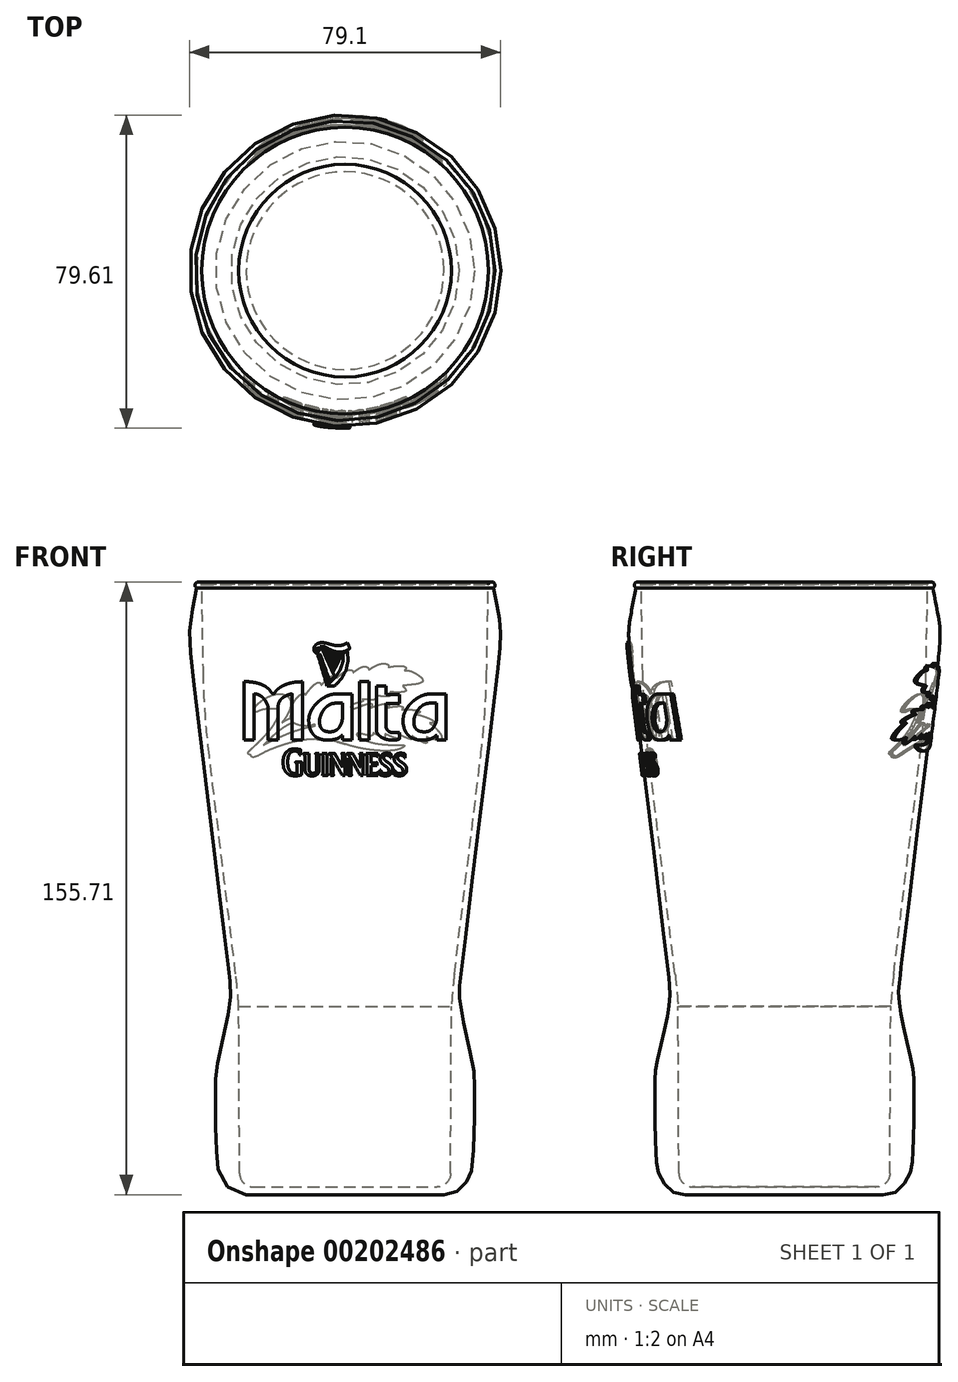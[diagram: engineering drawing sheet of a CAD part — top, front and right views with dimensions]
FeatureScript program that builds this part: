
annotation { "Feature Type Name" : "Feature", "Feature Type Description" : "" }
export const myFeature = defineFeature(function(context is Context, id is Id, definition is map)
    precondition{}
    {
        {
            var Q0;
            Q0=qCreatedBy(makeId("Front.planeOp"),FACE);
            var sketch = newSketch(context, id + "F0", { "sketchPlane" : qUnion([Q0])});
            skFitSpline(sketch, "E0", {"points": [v(-37.5, 79.86) * mm, v(-38.83, 73.29) * mm, v(-39.48, 68.91) * mm, v(-39.44, 64.6) * mm, v(-37.47, 47.15) * mm, v(-29.43, -19.33) * mm, v(-29.13, -22.16) * mm, v(-29.12, -25.92) * mm, v(-32.44, -42) * mm, v(-32.9, -47.3) * mm, v(-32.5, -66.8) * mm, v(-31.33, -71.06) * mm, v(-28.88, -74.03) * mm, v(-25.1, -75.12) * mm], "startDerivative": vector(-35.73, -160.8) * mm, "endDerivative": vector(111.11, -2.76) * mm});
            skLineSegment(sketch, "E1", {"start": v(-37.5, 79.86) * mm, "end": v(0, 79.86) * mm});
            skLineSegment(sketch, "E2", {"start": v(0, 79.86) * mm, "end": v(0, -75.12) * mm});
            skLineSegment(sketch, "E3", {"start": v(0, -75.12) * mm, "end": v(-25.1, -75.12) * mm});
            skSolve(sketch);
        }
        {
            var Q0;
            Q0=makeQuery(id+"F0.imprint","IMPRINT",FACE,{"disambiguationData":[TD([[makeQuery(id+"F0.imprint","IMPRINT",EDGE,{"derivedFrom":sQuery(id+"F0.wireOp",EDGE,"E0")}),1.0]])]});
            var Q1;
            Q1=sQuery(id+"F0.wireOp",EDGE,"E2");
            revolve(context, id + "F1", {"entities" : qUnion([Q0]), "axis" : qUnion([Q1]), "revolveType" : RevolveType.FULL});
        }
        {
            var Q0;
            Q0=qCreatedBy(makeId("Front.planeOp"),FACE);
            var sketch = newSketch(context, id + "F2", { "sketchPlane" : qUnion([Q0])});
            skLineSegment(sketch, "E4", {"start": v(0, 85.35) * mm, "end": v(-36.5, 85.35) * mm});
            skLineSegment(sketch, "E5", {"start": v(0, -73.16) * mm, "end": v(-23.31, -73.16) * mm});
            skLineSegment(sketch, "E6", {"start": v(0, 85.35) * mm, "end": v(0, -73.16) * mm});
            skLineSegment(sketch, "E7", {"start": v(-27.01, -27.28) * mm, "end": v(-26.8, -69.68) * mm});
            skLineSegment(sketch, "E8", {"start": v(-35.97, 56.7) * mm, "end": v(-36.5, 85.35) * mm});
            skLineSegment(sketch, "E9", {"start": v(-27.77, -19.08) * mm, "end": v(-34.48, 36.36) * mm});
            skArc(sketch, "E10", {"start": v(-27.01, -27.28) * mm, "mid": v(-27.34, -23.18) * mm, "end": v(-27.77, -19.08) * mm});
            skArc(sketch, "E11", {"start": v(-35.97, 56.7) * mm, "mid": v(-35.46, 46.51) * mm, "end": v(-34.48, 36.36) * mm});
            skPoint(sketch, "E12.visualSharp", {"position": v(-26.8, -73.16) * mm});
            skArc(sketch, "E12.filletArc", {"start": v(-26.8, -69.68) * mm, "mid": v(-25.78, -72.14) * mm, "end": v(-23.31, -73.16) * mm});
            skPoint(sketch, "E13.start.orphan", {"position": v(0, -75.16) * mm});
            skLineSegment(sketch, "E14", {"start": v(9.18, 85.35) * mm, "end": v(9.18, 79.96) * mm});
            skSolve(sketch);
        }
        {
            var Q0;
            Q0=qCreatedBy(makeId("Front.planeOp"),FACE);
            cPlane(context, id + "F3", {"entities" : qUnion([Q0]), "cplaneType" : CPlaneType.OFFSET, "offset" : 50 * mm, "width" : 150 * mm, "height" : 150 * mm});
        }
        {
            var Q0;
            Q0=makeQuery(id+"F2.imprint","IMPRINT",FACE,{"disambiguationData":[TD([[makeQuery(id+"F2.imprint","IMPRINT",EDGE,{"derivedFrom":sQuery(id+"F2.wireOp",EDGE,"E4")}),1.0]])]});
            var Q1;
            Q1=sQuery(id+"F2.wireOp",EDGE,"E6");
            revolve(context, id + "F4", {"operationType" : NewBodyOperationType.REMOVE, "entities" : qUnion([Q0]), "axis" : qUnion([Q1]), "revolveType" : RevolveType.FULL, "oppositeDirection" : true});
        }
        {
            var Q0;
            Q0=qCreatedBy(makeId("Front.planeOp"),FACE);
            var sketch = newSketch(context, id + "F5", { "sketchPlane" : qUnion([Q0])});
            skLineSegment(sketch, "E15", {"start": v(0, 79.96) * mm, "end": v(0, 86.28) * mm});
            skCircle(sketch, "E16", {"center": v(-37.25, 79.73) * mm, "radius": 0.85 * mm});
            skPoint(sketch, "E16.first.point", {"position": v(-36.4, 79.83) * mm});
            skPoint(sketch, "E16.second.point", {"position": v(-38.07, 79.5) * mm});
            skPoint(sketch, "E16.third.point", {"position": v(-38.1, 79.73) * mm});
            skSolve(sketch);
        }
        {
            var Q0;
            Q0=makeQuery(id+"F5.imprint","IMPRINT",FACE,{"disambiguationData":[TD([[makeQuery(id+"F5.imprint","IMPRINT",EDGE,{"derivedFrom":sQuery(id+"F5.wireOp",EDGE,"E16")}),1.0]])]});
            var Q1;
            Q1=sQuery(id+"F5.wireOp",EDGE,"E15");
            revolve(context, id + "F6", {"operationType" : NewBodyOperationType.ADD, "entities" : qUnion([Q0]), "axis" : qUnion([Q1]), "revolveType" : RevolveType.FULL});
        }
        {
            var Q0;
            Q0=qCreatedBy(makeId("Front.planeOp"),FACE);
            cPlane(context, id + "F7", {"entities" : qUnion([Q0]), "cplaneType" : CPlaneType.OFFSET, "offset" : 50 * mm, "oppositeDirection" : true, "width" : 150 * mm, "height" : 150 * mm});
        }
        {
            var Q0;
            Q0=qCreatedBy(id+"F3.planeOp",FACE);
            var sketch = newSketch(context, id + "F8", { "sketchPlane" : qUnion([Q0])});
            skLineSegment(sketch, "E17", {"start": v(-18.04, 52.15) * mm, "end": v(-18.51, 52.15) * mm});
            skLineSegment(sketch, "E18", {"start": v(-18.51, 52.15) * mm, "end": v(-19.27, 53.26) * mm});
            skLineSegment(sketch, "E19", {"start": v(-19.27, 53.26) * mm, "end": v(-20.3, 54.06) * mm});
            skLineSegment(sketch, "E20", {"start": v(-20.3, 54.06) * mm, "end": v(-21.46, 54.62) * mm});
            skLineSegment(sketch, "E21", {"start": v(-21.46, 54.62) * mm, "end": v(-22.68, 54.96) * mm});
            skLineSegment(sketch, "E22", {"start": v(-22.68, 54.96) * mm, "end": v(-23.82, 55.15) * mm});
            skLineSegment(sketch, "E23", {"start": v(-23.82, 55.15) * mm, "end": v(-24.77, 55.23) * mm});
            skLineSegment(sketch, "E24", {"start": v(-24.77, 55.23) * mm, "end": v(-25.42, 55.24) * mm});
            skLineSegment(sketch, "E25", {"start": v(-25.42, 55.24) * mm, "end": v(-25.66, 55.23) * mm});
            skLineSegment(sketch, "E26", {"start": v(-25.66, 55.23) * mm, "end": v(-25.66, 40.36) * mm});
            skLineSegment(sketch, "E27", {"start": v(-25.66, 40.36) * mm, "end": v(-23.13, 40.36) * mm});
            skLineSegment(sketch, "E28", {"start": v(-23.13, 40.36) * mm, "end": v(-23.13, 52.15) * mm});
            skLineSegment(sketch, "E29", {"start": v(-23.13, 52.15) * mm, "end": v(-22.2, 52) * mm});
            skLineSegment(sketch, "E30", {"start": v(-22.2, 52) * mm, "end": v(-21.43, 51.64) * mm});
            skLineSegment(sketch, "E31", {"start": v(-21.43, 51.64) * mm, "end": v(-20.8, 51.11) * mm});
            skLineSegment(sketch, "E32", {"start": v(-20.8, 51.11) * mm, "end": v(-20.33, 50.5) * mm});
            skLineSegment(sketch, "E33", {"start": v(-20.33, 50.5) * mm, "end": v(-19.97, 49.9) * mm});
            skLineSegment(sketch, "E34", {"start": v(-19.97, 49.9) * mm, "end": v(-19.74, 49.38) * mm});
            skLineSegment(sketch, "E35", {"start": v(-19.74, 49.38) * mm, "end": v(-19.6, 49) * mm});
            skLineSegment(sketch, "E36", {"start": v(-19.6, 49) * mm, "end": v(-19.56, 48.86) * mm});
            skLineSegment(sketch, "E37", {"start": v(-19.56, 48.86) * mm, "end": v(-19.56, 40.36) * mm});
            skLineSegment(sketch, "E38", {"start": v(-19.56, 40.36) * mm, "end": v(-17.05, 40.36) * mm});
            skLineSegment(sketch, "E39", {"start": v(-17.05, 40.36) * mm, "end": v(-17.05, 48.8) * mm});
            skLineSegment(sketch, "E40", {"start": v(-17.05, 48.8) * mm, "end": v(-16.9, 49.75) * mm});
            skLineSegment(sketch, "E41", {"start": v(-16.9, 49.75) * mm, "end": v(-16.5, 50.5) * mm});
            skLineSegment(sketch, "E42", {"start": v(-16.5, 50.5) * mm, "end": v(-15.91, 51.08) * mm});
            skLineSegment(sketch, "E43", {"start": v(-15.91, 51.08) * mm, "end": v(-15.25, 51.52) * mm});
            skLineSegment(sketch, "E44", {"start": v(-15.25, 51.52) * mm, "end": v(-14.6, 51.82) * mm});
            skLineSegment(sketch, "E45", {"start": v(-14.6, 51.82) * mm, "end": v(-14.01, 52.02) * mm});
            skLineSegment(sketch, "E46", {"start": v(-14.01, 52.02) * mm, "end": v(-13.6, 52.12) * mm});
            skLineSegment(sketch, "E47", {"start": v(-13.6, 52.12) * mm, "end": v(-13.45, 52.15) * mm});
            skLineSegment(sketch, "E48", {"start": v(-13.45, 52.15) * mm, "end": v(-13.45, 40.36) * mm});
            skLineSegment(sketch, "E49", {"start": v(-13.45, 40.36) * mm, "end": v(-10.79, 40.36) * mm});
            skLineSegment(sketch, "E50", {"start": v(-10.79, 40.36) * mm, "end": v(-10.79, 55.23) * mm});
            skLineSegment(sketch, "E51", {"start": v(-10.79, 55.23) * mm, "end": v(-12.8, 55.1) * mm});
            skLineSegment(sketch, "E52", {"start": v(-12.8, 55.1) * mm, "end": v(-14.41, 54.75) * mm});
            skLineSegment(sketch, "E53", {"start": v(-14.41, 54.75) * mm, "end": v(-15.68, 54.26) * mm});
            skLineSegment(sketch, "E54", {"start": v(-15.68, 54.26) * mm, "end": v(-16.63, 53.69) * mm});
            skLineSegment(sketch, "E55", {"start": v(-16.63, 53.69) * mm, "end": v(-17.3, 53.12) * mm});
            skLineSegment(sketch, "E56", {"start": v(-17.3, 53.12) * mm, "end": v(-17.74, 52.63) * mm});
            skLineSegment(sketch, "E57", {"start": v(-17.74, 52.63) * mm, "end": v(-17.97, 52.28) * mm});
            skLineSegment(sketch, "E58", {"start": v(-17.97, 52.28) * mm, "end": v(-18.04, 52.15) * mm});
            skLineSegment(sketch, "E59", {"start": v(-6.48, 45.4) * mm, "end": v(-6.43, 45.82) * mm});
            skLineSegment(sketch, "E60", {"start": v(-6.43, 45.82) * mm, "end": v(-6.26, 46.43) * mm});
            skLineSegment(sketch, "E61", {"start": v(-6.26, 46.43) * mm, "end": v(-5.97, 47.15) * mm});
            skLineSegment(sketch, "E62", {"start": v(-5.97, 47.15) * mm, "end": v(-5.54, 47.91) * mm});
            skLineSegment(sketch, "E63", {"start": v(-5.54, 47.91) * mm, "end": v(-4.96, 48.63) * mm});
            skLineSegment(sketch, "E64", {"start": v(-4.96, 48.63) * mm, "end": v(-4.23, 49.23) * mm});
            skLineSegment(sketch, "E65", {"start": v(-4.23, 49.23) * mm, "end": v(-3.33, 49.65) * mm});
            skLineSegment(sketch, "E66", {"start": v(-3.33, 49.65) * mm, "end": v(-2.26, 49.8) * mm});
            skLineSegment(sketch, "E67", {"start": v(-2.26, 49.8) * mm, "end": v(-0.67, 49.8) * mm});
            skLineSegment(sketch, "E68", {"start": v(-0.67, 49.8) * mm, "end": v(-0.67, 45.91) * mm});
            skLineSegment(sketch, "E69", {"start": v(-0.67, 45.91) * mm, "end": v(-0.68, 45.77) * mm});
            skLineSegment(sketch, "E70", {"start": v(-0.68, 45.77) * mm, "end": v(-0.75, 45.37) * mm});
            skLineSegment(sketch, "E71", {"start": v(-0.75, 45.37) * mm, "end": v(-0.9, 44.82) * mm});
            skLineSegment(sketch, "E72", {"start": v(-0.9, 44.82) * mm, "end": v(-1.14, 44.18) * mm});
            skLineSegment(sketch, "E73", {"start": v(-1.14, 44.18) * mm, "end": v(-1.53, 43.54) * mm});
            skLineSegment(sketch, "E74", {"start": v(-1.53, 43.54) * mm, "end": v(-2.07, 42.99) * mm});
            skLineSegment(sketch, "E75", {"start": v(-2.07, 42.99) * mm, "end": v(-2.81, 42.6) * mm});
            skLineSegment(sketch, "E76", {"start": v(-2.81, 42.6) * mm, "end": v(-3.77, 42.44) * mm});
            skLineSegment(sketch, "E77", {"start": v(-3.77, 42.44) * mm, "end": v(-4.71, 42.54) * mm});
            skLineSegment(sketch, "E78", {"start": v(-4.71, 42.54) * mm, "end": v(-5.4, 42.79) * mm});
            skLineSegment(sketch, "E79", {"start": v(-5.4, 42.79) * mm, "end": v(-5.9, 43.16) * mm});
            skLineSegment(sketch, "E80", {"start": v(-5.9, 43.16) * mm, "end": v(-6.2, 43.6) * mm});
            skLineSegment(sketch, "E81", {"start": v(-6.2, 43.6) * mm, "end": v(-6.38, 44.1) * mm});
            skLineSegment(sketch, "E82", {"start": v(-6.38, 44.1) * mm, "end": v(-6.46, 44.58) * mm});
            skLineSegment(sketch, "E83", {"start": v(-6.46, 44.58) * mm, "end": v(-6.49, 45.03) * mm});
            skLineSegment(sketch, "E84", {"start": v(-6.49, 45.03) * mm, "end": v(-6.48, 45.4) * mm});
            skLineSegment(sketch, "E85", {"start": v(-4.48, 40.35) * mm, "end": v(-3.5, 40.4) * mm});
            skLineSegment(sketch, "E86", {"start": v(-3.5, 40.4) * mm, "end": v(-2.73, 40.53) * mm});
            skLineSegment(sketch, "E87", {"start": v(-2.73, 40.53) * mm, "end": v(-2.11, 40.72) * mm});
            skLineSegment(sketch, "E88", {"start": v(-2.11, 40.72) * mm, "end": v(-1.65, 40.93) * mm});
            skLineSegment(sketch, "E89", {"start": v(-1.65, 40.93) * mm, "end": v(-1.32, 41.14) * mm});
            skLineSegment(sketch, "E90", {"start": v(-1.32, 41.14) * mm, "end": v(-1.1, 41.32) * mm});
            skLineSegment(sketch, "E91", {"start": v(-1.1, 41.32) * mm, "end": v(-0.99, 41.45) * mm});
            skLineSegment(sketch, "E92", {"start": v(-0.99, 41.45) * mm, "end": v(-0.95, 41.5) * mm});
            skLineSegment(sketch, "E93", {"start": v(-0.95, 41.5) * mm, "end": v(-0.61, 41.5) * mm});
            skLineSegment(sketch, "E94", {"start": v(-0.61, 41.5) * mm, "end": v(-0.61, 40.35) * mm});
            skLineSegment(sketch, "E95", {"start": v(-0.61, 40.35) * mm, "end": v(1.7, 40.35) * mm});
            skLineSegment(sketch, "E96", {"start": v(1.7, 40.35) * mm, "end": v(1.7, 52.1) * mm});
            skLineSegment(sketch, "E97", {"start": v(1.7, 52.1) * mm, "end": v(-2.57, 52.1) * mm});
            skLineSegment(sketch, "E98", {"start": v(-2.57, 52.1) * mm, "end": v(-3.6, 51.95) * mm});
            skLineSegment(sketch, "E99", {"start": v(-3.6, 51.95) * mm, "end": v(-4.72, 51.54) * mm});
            skLineSegment(sketch, "E100", {"start": v(-4.72, 51.54) * mm, "end": v(-5.83, 50.9) * mm});
            skLineSegment(sketch, "E101", {"start": v(-5.83, 50.9) * mm, "end": v(-6.89, 50.07) * mm});
            skLineSegment(sketch, "E102", {"start": v(-6.89, 50.07) * mm, "end": v(-7.82, 49.07) * mm});
            skLineSegment(sketch, "E103", {"start": v(-7.82, 49.07) * mm, "end": v(-8.57, 47.95) * mm});
            skLineSegment(sketch, "E104", {"start": v(-8.57, 47.95) * mm, "end": v(-9.07, 46.74) * mm});
            skLineSegment(sketch, "E105", {"start": v(-9.07, 46.74) * mm, "end": v(-9.25, 45.47) * mm});
            skLineSegment(sketch, "E106", {"start": v(-9.25, 45.47) * mm, "end": v(-9.16, 44.27) * mm});
            skLineSegment(sketch, "E107", {"start": v(-9.16, 44.27) * mm, "end": v(-8.9, 43.23) * mm});
            skLineSegment(sketch, "E108", {"start": v(-8.9, 43.23) * mm, "end": v(-8.49, 42.35) * mm});
            skLineSegment(sketch, "E109", {"start": v(-8.49, 42.35) * mm, "end": v(-7.93, 41.63) * mm});
            skLineSegment(sketch, "E110", {"start": v(-7.93, 41.63) * mm, "end": v(-7.24, 41.07) * mm});
            skLineSegment(sketch, "E111", {"start": v(-7.24, 41.07) * mm, "end": v(-6.42, 40.67) * mm});
            skLineSegment(sketch, "E112", {"start": v(-6.42, 40.67) * mm, "end": v(-5.5, 40.43) * mm});
            skLineSegment(sketch, "E113", {"start": v(-5.5, 40.43) * mm, "end": v(-4.48, 40.35) * mm});
            skLineSegment(sketch, "E114", {"start": v(3.61, 55.23) * mm, "end": v(6.07, 55.23) * mm});
            skLineSegment(sketch, "E115", {"start": v(6.07, 55.23) * mm, "end": v(6.07, 40.36) * mm});
            skLineSegment(sketch, "E116", {"start": v(6.07, 40.36) * mm, "end": v(3.61, 40.36) * mm});
            skLineSegment(sketch, "E117", {"start": v(3.61, 40.36) * mm, "end": v(3.61, 55.23) * mm});
            skLineSegment(sketch, "E118", {"start": v(13.84, 40.75) * mm, "end": v(13.84, 42.31) * mm});
            skLineSegment(sketch, "E119", {"start": v(13.84, 42.31) * mm, "end": v(11.94, 42.31) * mm});
            skLineSegment(sketch, "E120", {"start": v(11.94, 42.31) * mm, "end": v(11.46, 42.38) * mm});
            skLineSegment(sketch, "E121", {"start": v(11.46, 42.38) * mm, "end": v(11.08, 42.57) * mm});
            skLineSegment(sketch, "E122", {"start": v(11.08, 42.57) * mm, "end": v(10.8, 42.84) * mm});
            skLineSegment(sketch, "E123", {"start": v(10.8, 42.84) * mm, "end": v(10.6, 43.15) * mm});
            skLineSegment(sketch, "E124", {"start": v(10.6, 43.15) * mm, "end": v(10.47, 43.45) * mm});
            skLineSegment(sketch, "E125", {"start": v(10.47, 43.45) * mm, "end": v(10.4, 43.72) * mm});
            skLineSegment(sketch, "E126", {"start": v(10.4, 43.72) * mm, "end": v(10.36, 43.91) * mm});
            skLineSegment(sketch, "E127", {"start": v(10.36, 43.91) * mm, "end": v(10.35, 43.98) * mm});
            skLineSegment(sketch, "E128", {"start": v(10.35, 43.98) * mm, "end": v(10.35, 49.7) * mm});
            skLineSegment(sketch, "E129", {"start": v(10.35, 49.7) * mm, "end": v(13.84, 49.7) * mm});
            skLineSegment(sketch, "E130", {"start": v(13.84, 49.7) * mm, "end": v(13.84, 51.97) * mm});
            skLineSegment(sketch, "E131", {"start": v(13.84, 51.97) * mm, "end": v(10.37, 51.97) * mm});
            skLineSegment(sketch, "E132", {"start": v(10.37, 51.97) * mm, "end": v(10.37, 54.1) * mm});
            skLineSegment(sketch, "E133", {"start": v(10.37, 54.1) * mm, "end": v(7.95, 54.1) * mm});
            skLineSegment(sketch, "E134", {"start": v(7.95, 54.1) * mm, "end": v(7.95, 43) * mm});
            skLineSegment(sketch, "E135", {"start": v(7.95, 43) * mm, "end": v(8.05, 42.38) * mm});
            skLineSegment(sketch, "E136", {"start": v(8.05, 42.38) * mm, "end": v(8.35, 41.84) * mm});
            skLineSegment(sketch, "E137", {"start": v(8.35, 41.84) * mm, "end": v(8.8, 41.39) * mm});
            skLineSegment(sketch, "E138", {"start": v(8.8, 41.39) * mm, "end": v(9.36, 41.02) * mm});
            skLineSegment(sketch, "E139", {"start": v(9.36, 41.02) * mm, "end": v(10, 40.73) * mm});
            skLineSegment(sketch, "E140", {"start": v(10, 40.73) * mm, "end": v(10.66, 40.52) * mm});
            skLineSegment(sketch, "E141", {"start": v(10.66, 40.52) * mm, "end": v(11.33, 40.4) * mm});
            skLineSegment(sketch, "E142", {"start": v(11.33, 40.4) * mm, "end": v(11.96, 40.35) * mm});
            skLineSegment(sketch, "E143", {"start": v(11.96, 40.35) * mm, "end": v(12.5, 40.37) * mm});
            skLineSegment(sketch, "E144", {"start": v(12.5, 40.37) * mm, "end": v(12.93, 40.42) * mm});
            skLineSegment(sketch, "E145", {"start": v(12.93, 40.42) * mm, "end": v(13.26, 40.48) * mm});
            skLineSegment(sketch, "E146", {"start": v(13.26, 40.48) * mm, "end": v(13.5, 40.55) * mm});
            skLineSegment(sketch, "E147", {"start": v(13.5, 40.55) * mm, "end": v(13.67, 40.62) * mm});
            skLineSegment(sketch, "E148", {"start": v(13.67, 40.62) * mm, "end": v(13.77, 40.69) * mm});
            skLineSegment(sketch, "E149", {"start": v(13.77, 40.69) * mm, "end": v(13.83, 40.73) * mm});
            skLineSegment(sketch, "E150", {"start": v(13.83, 40.73) * mm, "end": v(13.84, 40.75) * mm});
            skLineSegment(sketch, "E151", {"start": v(-4.88, 61.42) * mm, "end": v(-4.83, 61.5) * mm});
            skLineSegment(sketch, "E152", {"start": v(-4.83, 61.5) * mm, "end": v(-4.7, 61.7) * mm});
            skLineSegment(sketch, "E153", {"start": v(-4.7, 61.7) * mm, "end": v(-4.54, 62) * mm});
            skLineSegment(sketch, "E154", {"start": v(-4.54, 62) * mm, "end": v(-4.34, 62.39) * mm});
            skLineSegment(sketch, "E155", {"start": v(-4.34, 62.39) * mm, "end": v(-4.18, 62.8) * mm});
            skLineSegment(sketch, "E156", {"start": v(-4.18, 62.8) * mm, "end": v(-4.06, 63.12) * mm});
            skLineSegment(sketch, "E157", {"start": v(-4.06, 63.12) * mm, "end": v(-4, 63.34) * mm});
            skLineSegment(sketch, "E158", {"start": v(-4, 63.34) * mm, "end": v(-3.97, 63.43) * mm});
            skLineSegment(sketch, "E159", {"start": v(-3.97, 63.43) * mm, "end": v(-4.03, 63.35) * mm});
            skLineSegment(sketch, "E160", {"start": v(-4.03, 63.35) * mm, "end": v(-4.15, 63.16) * mm});
            skLineSegment(sketch, "E161", {"start": v(-4.15, 63.16) * mm, "end": v(-4.32, 62.86) * mm});
            skLineSegment(sketch, "E162", {"start": v(-4.32, 62.86) * mm, "end": v(-4.51, 62.47) * mm});
            skLineSegment(sketch, "E163", {"start": v(-4.51, 62.47) * mm, "end": v(-4.68, 62.06) * mm});
            skLineSegment(sketch, "E164", {"start": v(-4.68, 62.06) * mm, "end": v(-4.8, 61.74) * mm});
            skLineSegment(sketch, "E165", {"start": v(-4.8, 61.74) * mm, "end": v(-4.86, 61.51) * mm});
            skLineSegment(sketch, "E166", {"start": v(-4.86, 61.51) * mm, "end": v(-4.88, 61.42) * mm});
            skLineSegment(sketch, "E167", {"start": v(-4.42, 63.67) * mm, "end": v(-4.47, 63.6) * mm});
            skLineSegment(sketch, "E168", {"start": v(-4.47, 63.6) * mm, "end": v(-4.57, 63.45) * mm});
            skLineSegment(sketch, "E169", {"start": v(-4.57, 63.45) * mm, "end": v(-4.7, 63.2) * mm});
            skLineSegment(sketch, "E170", {"start": v(-4.7, 63.2) * mm, "end": v(-4.86, 62.89) * mm});
            skLineSegment(sketch, "E171", {"start": v(-4.86, 62.89) * mm, "end": v(-5, 62.56) * mm});
            skLineSegment(sketch, "E172", {"start": v(-5, 62.56) * mm, "end": v(-5.1, 62.3) * mm});
            skLineSegment(sketch, "E173", {"start": v(-5.1, 62.3) * mm, "end": v(-5.14, 62.11) * mm});
            skLineSegment(sketch, "E174", {"start": v(-5.14, 62.11) * mm, "end": v(-5.16, 62.04) * mm});
            skLineSegment(sketch, "E175", {"start": v(-5.16, 62.04) * mm, "end": v(-5.12, 62.1) * mm});
            skLineSegment(sketch, "E176", {"start": v(-5.12, 62.1) * mm, "end": v(-5.02, 62.26) * mm});
            skLineSegment(sketch, "E177", {"start": v(-5.02, 62.26) * mm, "end": v(-4.88, 62.5) * mm});
            skLineSegment(sketch, "E178", {"start": v(-4.88, 62.5) * mm, "end": v(-4.72, 62.82) * mm});
            skLineSegment(sketch, "E179", {"start": v(-4.72, 62.82) * mm, "end": v(-4.58, 63.15) * mm});
            skLineSegment(sketch, "E180", {"start": v(-4.58, 63.15) * mm, "end": v(-4.5, 63.41) * mm});
            skLineSegment(sketch, "E181", {"start": v(-4.5, 63.41) * mm, "end": v(-4.44, 63.6) * mm});
            skLineSegment(sketch, "E182", {"start": v(-4.44, 63.6) * mm, "end": v(-4.42, 63.67) * mm});
            skLineSegment(sketch, "E183", {"start": v(-4.84, 63.9) * mm, "end": v(-4.88, 63.85) * mm});
            skLineSegment(sketch, "E184", {"start": v(-4.88, 63.85) * mm, "end": v(-4.96, 63.72) * mm});
            skLineSegment(sketch, "E185", {"start": v(-4.96, 63.72) * mm, "end": v(-5.07, 63.53) * mm});
            skLineSegment(sketch, "E186", {"start": v(-5.07, 63.53) * mm, "end": v(-5.2, 63.28) * mm});
            skLineSegment(sketch, "E187", {"start": v(-5.2, 63.28) * mm, "end": v(-5.3, 63.03) * mm});
            skLineSegment(sketch, "E188", {"start": v(-5.3, 63.03) * mm, "end": v(-5.37, 62.82) * mm});
            skLineSegment(sketch, "E189", {"start": v(-5.37, 62.82) * mm, "end": v(-5.41, 62.67) * mm});
            skLineSegment(sketch, "E190", {"start": v(-5.41, 62.67) * mm, "end": v(-5.43, 62.61) * mm});
            skLineSegment(sketch, "E191", {"start": v(-5.43, 62.61) * mm, "end": v(-5.4, 62.66) * mm});
            skLineSegment(sketch, "E192", {"start": v(-5.4, 62.66) * mm, "end": v(-5.3, 62.79) * mm});
            skLineSegment(sketch, "E193", {"start": v(-5.3, 62.79) * mm, "end": v(-5.2, 62.98) * mm});
            skLineSegment(sketch, "E194", {"start": v(-5.2, 62.98) * mm, "end": v(-5.07, 63.23) * mm});
            skLineSegment(sketch, "E195", {"start": v(-5.07, 63.23) * mm, "end": v(-4.97, 63.49) * mm});
            skLineSegment(sketch, "E196", {"start": v(-4.97, 63.49) * mm, "end": v(-4.9, 63.7) * mm});
            skLineSegment(sketch, "E197", {"start": v(-4.9, 63.7) * mm, "end": v(-4.86, 63.84) * mm});
            skLineSegment(sketch, "E198", {"start": v(-4.86, 63.84) * mm, "end": v(-4.84, 63.9) * mm});
            skLineSegment(sketch, "E199", {"start": v(-3.48, 63.2) * mm, "end": v(-3.55, 63.11) * mm});
            skLineSegment(sketch, "E200", {"start": v(-3.55, 63.11) * mm, "end": v(-3.7, 62.88) * mm});
            skLineSegment(sketch, "E201", {"start": v(-3.7, 62.88) * mm, "end": v(-3.9, 62.51) * mm});
            skLineSegment(sketch, "E202", {"start": v(-3.9, 62.51) * mm, "end": v(-4.14, 62.04) * mm});
            skLineSegment(sketch, "E203", {"start": v(-4.14, 62.04) * mm, "end": v(-4.34, 61.55) * mm});
            skLineSegment(sketch, "E204", {"start": v(-4.34, 61.55) * mm, "end": v(-4.48, 61.16) * mm});
            skLineSegment(sketch, "E205", {"start": v(-4.48, 61.16) * mm, "end": v(-4.56, 60.89) * mm});
            skLineSegment(sketch, "E206", {"start": v(-4.56, 60.89) * mm, "end": v(-4.59, 60.77) * mm});
            skLineSegment(sketch, "E207", {"start": v(-4.59, 60.77) * mm, "end": v(-4.59, 60.77) * mm});
            skLineSegment(sketch, "E208", {"start": v(-4.59, 60.77) * mm, "end": v(-4.52, 60.87) * mm});
            skLineSegment(sketch, "E209", {"start": v(-4.52, 60.87) * mm, "end": v(-4.37, 61.1) * mm});
            skLineSegment(sketch, "E210", {"start": v(-4.37, 61.1) * mm, "end": v(-4.16, 61.47) * mm});
            skLineSegment(sketch, "E211", {"start": v(-4.16, 61.47) * mm, "end": v(-3.93, 61.94) * mm});
            skLineSegment(sketch, "E212", {"start": v(-3.93, 61.94) * mm, "end": v(-3.73, 62.43) * mm});
            skLineSegment(sketch, "E213", {"start": v(-3.73, 62.43) * mm, "end": v(-3.59, 62.83) * mm});
            skLineSegment(sketch, "E214", {"start": v(-3.59, 62.83) * mm, "end": v(-3.5, 63.1) * mm});
            skLineSegment(sketch, "E215", {"start": v(-3.5, 63.1) * mm, "end": v(-3.48, 63.2) * mm});
            skLineSegment(sketch, "E216", {"start": v(-3.73, 61.58) * mm, "end": v(-3.97, 61) * mm});
            skLineSegment(sketch, "E217", {"start": v(-3.97, 61) * mm, "end": v(-4.14, 60.53) * mm});
            skLineSegment(sketch, "E218", {"start": v(-4.14, 60.53) * mm, "end": v(-4.23, 60.2) * mm});
            skLineSegment(sketch, "E219", {"start": v(-4.23, 60.2) * mm, "end": v(-4.27, 60.07) * mm});
            skLineSegment(sketch, "E220", {"start": v(-4.27, 60.07) * mm, "end": v(-4.27, 60.07) * mm});
            skLineSegment(sketch, "E221", {"start": v(-4.27, 60.07) * mm, "end": v(-4.19, 60.18) * mm});
            skLineSegment(sketch, "E222", {"start": v(-4.19, 60.18) * mm, "end": v(-4, 60.47) * mm});
            skLineSegment(sketch, "E223", {"start": v(-4, 60.47) * mm, "end": v(-3.76, 60.9) * mm});
            skLineSegment(sketch, "E224", {"start": v(-3.76, 60.9) * mm, "end": v(-3.48, 61.47) * mm});
            skLineSegment(sketch, "E225", {"start": v(-3.48, 61.47) * mm, "end": v(-3.24, 62.06) * mm});
            skLineSegment(sketch, "E226", {"start": v(-3.24, 62.06) * mm, "end": v(-3.07, 62.53) * mm});
            skLineSegment(sketch, "E227", {"start": v(-3.07, 62.53) * mm, "end": v(-2.97, 62.86) * mm});
            skLineSegment(sketch, "E228", {"start": v(-2.97, 62.86) * mm, "end": v(-2.94, 63) * mm});
            skLineSegment(sketch, "E229", {"start": v(-2.94, 63) * mm, "end": v(-2.94, 63) * mm});
            skLineSegment(sketch, "E230", {"start": v(-2.94, 63) * mm, "end": v(-3.02, 62.88) * mm});
            skLineSegment(sketch, "E231", {"start": v(-3.02, 62.88) * mm, "end": v(-3.2, 62.6) * mm});
            skLineSegment(sketch, "E232", {"start": v(-3.2, 62.6) * mm, "end": v(-3.45, 62.15) * mm});
            skLineSegment(sketch, "E233", {"start": v(-3.45, 62.15) * mm, "end": v(-3.73, 61.58) * mm});
            skLineSegment(sketch, "E234", {"start": v(-4.16, 54.7) * mm, "end": v(-6.57, 62.07) * mm});
            skLineSegment(sketch, "E235", {"start": v(-6.57, 62.07) * mm, "end": v(-6.72, 62.17) * mm});
            skLineSegment(sketch, "E236", {"start": v(-6.72, 62.17) * mm, "end": v(-6.83, 62.13) * mm});
            skLineSegment(sketch, "E237", {"start": v(-6.83, 62.13) * mm, "end": v(-6.87, 62.03) * mm});
            skLineSegment(sketch, "E238", {"start": v(-6.87, 62.03) * mm, "end": v(-6.85, 61.89) * mm});
            skLineSegment(sketch, "E239", {"start": v(-6.85, 61.89) * mm, "end": v(-6.8, 61.74) * mm});
            skLineSegment(sketch, "E240", {"start": v(-6.8, 61.74) * mm, "end": v(-4.56, 54.12) * mm});
            skLineSegment(sketch, "E241", {"start": v(-4.56, 54.12) * mm, "end": v(-2.66, 54.12) * mm});
            skLineSegment(sketch, "E242", {"start": v(-2.66, 54.12) * mm, "end": v(-0.9, 56) * mm});
            skLineSegment(sketch, "E243", {"start": v(-0.9, 56) * mm, "end": v(0.24, 58.13) * mm});
            skLineSegment(sketch, "E244", {"start": v(0.24, 58.13) * mm, "end": v(0.76, 60.46) * mm});
            skLineSegment(sketch, "E245", {"start": v(0.76, 60.46) * mm, "end": v(0.63, 62.94) * mm});
            skLineSegment(sketch, "E246", {"start": v(0.63, 62.94) * mm, "end": v(0.12, 62.72) * mm});
            skLineSegment(sketch, "E247", {"start": v(0.12, 62.72) * mm, "end": v(-0.44, 62.55) * mm});
            skLineSegment(sketch, "E248", {"start": v(-0.44, 62.55) * mm, "end": v(-0.56, 60.27) * mm});
            skLineSegment(sketch, "E249", {"start": v(-0.56, 60.27) * mm, "end": v(-1.24, 58.2) * mm});
            skLineSegment(sketch, "E250", {"start": v(-1.24, 58.2) * mm, "end": v(-2.46, 56.36) * mm});
            skLineSegment(sketch, "E251", {"start": v(-2.46, 56.36) * mm, "end": v(-4.16, 54.7) * mm});
            skLineSegment(sketch, "E252", {"start": v(-6.87, 63.76) * mm, "end": v(-6.71, 63.73) * mm});
            skLineSegment(sketch, "E253", {"start": v(-6.71, 63.73) * mm, "end": v(-6.58, 63.64) * mm});
            skLineSegment(sketch, "E254", {"start": v(-6.58, 63.64) * mm, "end": v(-6.5, 63.5) * mm});
            skLineSegment(sketch, "E255", {"start": v(-6.5, 63.5) * mm, "end": v(-6.46, 63.35) * mm});
            skLineSegment(sketch, "E256", {"start": v(-6.46, 63.35) * mm, "end": v(-6.5, 63.2) * mm});
            skLineSegment(sketch, "E257", {"start": v(-6.5, 63.2) * mm, "end": v(-6.58, 63.06) * mm});
            skLineSegment(sketch, "E258", {"start": v(-6.58, 63.06) * mm, "end": v(-6.71, 62.98) * mm});
            skLineSegment(sketch, "E259", {"start": v(-6.71, 62.98) * mm, "end": v(-6.87, 62.94) * mm});
            skLineSegment(sketch, "E260", {"start": v(-6.87, 62.94) * mm, "end": v(-7.03, 62.98) * mm});
            skLineSegment(sketch, "E261", {"start": v(-7.03, 62.98) * mm, "end": v(-7.16, 63.06) * mm});
            skLineSegment(sketch, "E262", {"start": v(-7.16, 63.06) * mm, "end": v(-7.25, 63.2) * mm});
            skLineSegment(sketch, "E263", {"start": v(-7.25, 63.2) * mm, "end": v(-7.28, 63.35) * mm});
            skLineSegment(sketch, "E264", {"start": v(-7.28, 63.35) * mm, "end": v(-7.25, 63.5) * mm});
            skLineSegment(sketch, "E265", {"start": v(-7.25, 63.5) * mm, "end": v(-7.16, 63.64) * mm});
            skLineSegment(sketch, "E266", {"start": v(-7.16, 63.64) * mm, "end": v(-7.03, 63.73) * mm});
            skLineSegment(sketch, "E267", {"start": v(-7.03, 63.73) * mm, "end": v(-6.87, 63.76) * mm});
            skLineSegment(sketch, "E268", {"start": v(-6.84, 62.33) * mm, "end": v(-6.43, 62.41) * mm});
            skLineSegment(sketch, "E269", {"start": v(-6.43, 62.41) * mm, "end": v(-3.88, 55.4) * mm});
            skLineSegment(sketch, "E270", {"start": v(-3.88, 55.4) * mm, "end": v(-3.63, 55.62) * mm});
            skLineSegment(sketch, "E271", {"start": v(-3.63, 55.62) * mm, "end": v(-3.25, 56) * mm});
            skLineSegment(sketch, "E272", {"start": v(-3.25, 56) * mm, "end": v(-2.85, 56.42) * mm});
            skLineSegment(sketch, "E273", {"start": v(-2.85, 56.42) * mm, "end": v(-2.56, 56.78) * mm});
            skLineSegment(sketch, "E274", {"start": v(-2.56, 56.78) * mm, "end": v(-2.76, 56.88) * mm});
            skLineSegment(sketch, "E275", {"start": v(-2.76, 56.88) * mm, "end": v(-2.91, 57.09) * mm});
            skLineSegment(sketch, "E276", {"start": v(-2.91, 57.09) * mm, "end": v(-2.98, 57.23) * mm});
            skLineSegment(sketch, "E277", {"start": v(-2.98, 57.23) * mm, "end": v(-3.15, 57.6) * mm});
            skLineSegment(sketch, "E278", {"start": v(-3.15, 57.6) * mm, "end": v(-3.01, 57.8) * mm});
            skLineSegment(sketch, "E279", {"start": v(-3.01, 57.8) * mm, "end": v(-2.7, 58.31) * mm});
            skLineSegment(sketch, "E280", {"start": v(-2.7, 58.31) * mm, "end": v(-2.27, 59.09) * mm});
            skLineSegment(sketch, "E281", {"start": v(-2.27, 59.09) * mm, "end": v(-1.79, 60.1) * mm});
            skLineSegment(sketch, "E282", {"start": v(-1.79, 60.1) * mm, "end": v(-1.35, 61.12) * mm});
            skLineSegment(sketch, "E283", {"start": v(-1.35, 61.12) * mm, "end": v(-1.05, 61.95) * mm});
            skLineSegment(sketch, "E284", {"start": v(-1.05, 61.95) * mm, "end": v(-0.88, 62.52) * mm});
            skLineSegment(sketch, "E285", {"start": v(-0.88, 62.52) * mm, "end": v(-0.81, 62.75) * mm});
            skLineSegment(sketch, "E286", {"start": v(-0.81, 62.75) * mm, "end": v(-0.95, 62.55) * mm});
            skLineSegment(sketch, "E287", {"start": v(-0.95, 62.55) * mm, "end": v(-1.26, 62.05) * mm});
            skLineSegment(sketch, "E288", {"start": v(-1.26, 62.05) * mm, "end": v(-1.69, 61.27) * mm});
            skLineSegment(sketch, "E289", {"start": v(-1.69, 61.27) * mm, "end": v(-2.17, 60.26) * mm});
            skLineSegment(sketch, "E290", {"start": v(-2.17, 60.26) * mm, "end": v(-2.6, 59.24) * mm});
            skLineSegment(sketch, "E291", {"start": v(-2.6, 59.24) * mm, "end": v(-2.9, 58.4) * mm});
            skLineSegment(sketch, "E292", {"start": v(-2.9, 58.4) * mm, "end": v(-3.09, 57.84) * mm});
            skLineSegment(sketch, "E293", {"start": v(-3.09, 57.84) * mm, "end": v(-3.15, 57.6) * mm});
            skLineSegment(sketch, "E294", {"start": v(-3.15, 57.6) * mm, "end": v(-3.33, 58) * mm});
            skLineSegment(sketch, "E295", {"start": v(-3.33, 58) * mm, "end": v(-3.55, 58.5) * mm});
            skLineSegment(sketch, "E296", {"start": v(-3.55, 58.5) * mm, "end": v(-3.44, 58.66) * mm});
            skLineSegment(sketch, "E297", {"start": v(-3.44, 58.66) * mm, "end": v(-3.18, 59.07) * mm});
            skLineSegment(sketch, "E298", {"start": v(-3.18, 59.07) * mm, "end": v(-2.82, 59.7) * mm});
            skLineSegment(sketch, "E299", {"start": v(-2.82, 59.7) * mm, "end": v(-2.42, 60.52) * mm});
            skLineSegment(sketch, "E300", {"start": v(-2.42, 60.52) * mm, "end": v(-2.07, 61.37) * mm});
            skLineSegment(sketch, "E301", {"start": v(-2.07, 61.37) * mm, "end": v(-1.83, 62.05) * mm});
            skLineSegment(sketch, "E302", {"start": v(-1.83, 62.05) * mm, "end": v(-1.69, 62.52) * mm});
            skLineSegment(sketch, "E303", {"start": v(-1.69, 62.52) * mm, "end": v(-1.64, 62.7) * mm});
            skLineSegment(sketch, "E304", {"start": v(-1.64, 62.7) * mm, "end": v(-1.75, 62.55) * mm});
            skLineSegment(sketch, "E305", {"start": v(-1.75, 62.55) * mm, "end": v(-2, 62.13) * mm});
            skLineSegment(sketch, "E306", {"start": v(-2, 62.13) * mm, "end": v(-2.36, 61.5) * mm});
            skLineSegment(sketch, "E307", {"start": v(-2.36, 61.5) * mm, "end": v(-2.76, 60.68) * mm});
            skLineSegment(sketch, "E308", {"start": v(-2.76, 60.68) * mm, "end": v(-3.12, 59.84) * mm});
            skLineSegment(sketch, "E309", {"start": v(-3.12, 59.84) * mm, "end": v(-3.36, 59.16) * mm});
            skLineSegment(sketch, "E310", {"start": v(-3.36, 59.16) * mm, "end": v(-3.5, 58.69) * mm});
            skLineSegment(sketch, "E311", {"start": v(-3.5, 58.69) * mm, "end": v(-3.55, 58.5) * mm});
            skLineSegment(sketch, "E312", {"start": v(-3.55, 58.5) * mm, "end": v(-3.92, 59.31) * mm});
            skLineSegment(sketch, "E313", {"start": v(-3.92, 59.31) * mm, "end": v(-3.83, 59.45) * mm});
            skLineSegment(sketch, "E314", {"start": v(-3.83, 59.45) * mm, "end": v(-3.61, 59.8) * mm});
            skLineSegment(sketch, "E315", {"start": v(-3.61, 59.8) * mm, "end": v(-3.32, 60.31) * mm});
            skLineSegment(sketch, "E316", {"start": v(-3.32, 60.31) * mm, "end": v(-2.99, 61) * mm});
            skLineSegment(sketch, "E317", {"start": v(-2.99, 61) * mm, "end": v(-2.7, 61.7) * mm});
            skLineSegment(sketch, "E318", {"start": v(-2.7, 61.7) * mm, "end": v(-2.5, 62.26) * mm});
            skLineSegment(sketch, "E319", {"start": v(-2.5, 62.26) * mm, "end": v(-2.38, 62.65) * mm});
            skLineSegment(sketch, "E320", {"start": v(-2.38, 62.65) * mm, "end": v(-2.34, 62.81) * mm});
            skLineSegment(sketch, "E321", {"start": v(-2.34, 62.81) * mm, "end": v(-2.43, 62.68) * mm});
            skLineSegment(sketch, "E322", {"start": v(-2.43, 62.68) * mm, "end": v(-2.64, 62.33) * mm});
            skLineSegment(sketch, "E323", {"start": v(-2.64, 62.33) * mm, "end": v(-2.94, 61.8) * mm});
            skLineSegment(sketch, "E324", {"start": v(-2.94, 61.8) * mm, "end": v(-3.27, 61.13) * mm});
            skLineSegment(sketch, "E325", {"start": v(-3.27, 61.13) * mm, "end": v(-3.57, 60.43) * mm});
            skLineSegment(sketch, "E326", {"start": v(-3.57, 60.43) * mm, "end": v(-3.77, 59.86) * mm});
            skLineSegment(sketch, "E327", {"start": v(-3.77, 59.86) * mm, "end": v(-3.88, 59.47) * mm});
            skLineSegment(sketch, "E328", {"start": v(-3.88, 59.47) * mm, "end": v(-3.92, 59.31) * mm});
            skLineSegment(sketch, "E329", {"start": v(-3.92, 59.31) * mm, "end": v(-4.27, 60.07) * mm});
            skLineSegment(sketch, "E330", {"start": v(-4.27, 60.07) * mm, "end": v(-4.59, 60.77) * mm});
            skLineSegment(sketch, "E331", {"start": v(-4.59, 60.77) * mm, "end": v(-5.04, 61.77) * mm});
            skLineSegment(sketch, "E332", {"start": v(-5.04, 61.77) * mm, "end": v(-5.43, 62.61) * mm});
            skLineSegment(sketch, "E333", {"start": v(-5.43, 62.61) * mm, "end": v(-5.43, 62.61) * mm});
            skLineSegment(sketch, "E334", {"start": v(-5.43, 62.61) * mm, "end": v(-5.66, 63.12) * mm});
            skLineSegment(sketch, "E335", {"start": v(-5.66, 63.12) * mm, "end": v(-5.77, 63.38) * mm});
            skLineSegment(sketch, "E336", {"start": v(-5.77, 63.38) * mm, "end": v(-6.01, 63.87) * mm});
            skLineSegment(sketch, "E337", {"start": v(-6.01, 63.87) * mm, "end": v(-6.3, 64.15) * mm});
            skLineSegment(sketch, "E338", {"start": v(-6.3, 64.15) * mm, "end": v(-5.8, 64.2) * mm});
            skLineSegment(sketch, "E339", {"start": v(-5.8, 64.2) * mm, "end": v(-5.22, 64.08) * mm});
            skLineSegment(sketch, "E340", {"start": v(-5.22, 64.08) * mm, "end": v(-4.84, 63.9) * mm});
            skLineSegment(sketch, "E341", {"start": v(-4.84, 63.9) * mm, "end": v(-4.84, 63.9) * mm});
            skLineSegment(sketch, "E342", {"start": v(-4.84, 63.9) * mm, "end": v(-4.26, 63.59) * mm});
            skLineSegment(sketch, "E343", {"start": v(-4.26, 63.59) * mm, "end": v(-3.55, 63.24) * mm});
            skLineSegment(sketch, "E344", {"start": v(-3.55, 63.24) * mm, "end": v(-2.94, 63) * mm});
            skLineSegment(sketch, "E345", {"start": v(-2.94, 63) * mm, "end": v(-2.25, 62.8) * mm});
            skLineSegment(sketch, "E346", {"start": v(-2.25, 62.8) * mm, "end": v(-1.59, 62.7) * mm});
            skLineSegment(sketch, "E347", {"start": v(-1.59, 62.7) * mm, "end": v(-0.8, 62.75) * mm});
            skLineSegment(sketch, "E348", {"start": v(-0.8, 62.75) * mm, "end": v(-0.02, 62.95) * mm});
            skLineSegment(sketch, "E349", {"start": v(-0.02, 62.95) * mm, "end": v(0.67, 63.26) * mm});
            skLineSegment(sketch, "E350", {"start": v(0.67, 63.26) * mm, "end": v(1.21, 63.66) * mm});
            skLineSegment(sketch, "E351", {"start": v(1.21, 63.66) * mm, "end": v(0.64, 65.15) * mm});
            skLineSegment(sketch, "E352", {"start": v(0.64, 65.15) * mm, "end": v(-0.22, 64.65) * mm});
            skLineSegment(sketch, "E353", {"start": v(-0.22, 64.65) * mm, "end": v(-1.28, 64.38) * mm});
            skLineSegment(sketch, "E354", {"start": v(-1.28, 64.38) * mm, "end": v(-2.5, 64.4) * mm});
            skLineSegment(sketch, "E355", {"start": v(-2.5, 64.4) * mm, "end": v(-3.85, 64.75) * mm});
            skLineSegment(sketch, "E356", {"start": v(-3.85, 64.75) * mm, "end": v(-4.89, 65.05) * mm});
            skLineSegment(sketch, "E357", {"start": v(-4.89, 65.05) * mm, "end": v(-5.78, 65.15) * mm});
            skLineSegment(sketch, "E358", {"start": v(-5.78, 65.15) * mm, "end": v(-6.28, 65.11) * mm});
            skLineSegment(sketch, "E359", {"start": v(-6.28, 65.11) * mm, "end": v(-6.72, 65) * mm});
            skLineSegment(sketch, "E360", {"start": v(-6.72, 65) * mm, "end": v(-7.09, 64.85) * mm});
            skLineSegment(sketch, "E361", {"start": v(-7.09, 64.85) * mm, "end": v(-7.39, 64.64) * mm});
            skLineSegment(sketch, "E362", {"start": v(-7.39, 64.64) * mm, "end": v(-7.62, 64.4) * mm});
            skLineSegment(sketch, "E363", {"start": v(-7.62, 64.4) * mm, "end": v(-7.8, 64.11) * mm});
            skLineSegment(sketch, "E364", {"start": v(-7.8, 64.11) * mm, "end": v(-7.9, 63.8) * mm});
            skLineSegment(sketch, "E365", {"start": v(-7.9, 63.8) * mm, "end": v(-7.93, 63.5) * mm});
            skLineSegment(sketch, "E366", {"start": v(-7.93, 63.5) * mm, "end": v(-7.85, 63.02) * mm});
            skLineSegment(sketch, "E367", {"start": v(-7.85, 63.02) * mm, "end": v(-7.62, 62.65) * mm});
            skLineSegment(sketch, "E368", {"start": v(-7.62, 62.65) * mm, "end": v(-7.27, 62.41) * mm});
            skLineSegment(sketch, "E369", {"start": v(-7.27, 62.41) * mm, "end": v(-6.84, 62.33) * mm});
            skLineSegment(sketch, "E370", {"start": v(14.57, 34.6) * mm, "end": v(14.02, 34.97) * mm});
            skLineSegment(sketch, "E371", {"start": v(14.02, 34.97) * mm, "end": v(13.5, 35.43) * mm});
            skLineSegment(sketch, "E372", {"start": v(13.5, 35.43) * mm, "end": v(13.34, 35.9) * mm});
            skLineSegment(sketch, "E373", {"start": v(13.34, 35.9) * mm, "end": v(13.38, 36.16) * mm});
            skLineSegment(sketch, "E374", {"start": v(13.38, 36.16) * mm, "end": v(13.52, 36.37) * mm});
            skLineSegment(sketch, "E375", {"start": v(13.52, 36.37) * mm, "end": v(13.75, 36.5) * mm});
            skLineSegment(sketch, "E376", {"start": v(13.75, 36.5) * mm, "end": v(14.1, 36.56) * mm});
            skLineSegment(sketch, "E377", {"start": v(14.1, 36.56) * mm, "end": v(14.48, 36.5) * mm});
            skLineSegment(sketch, "E378", {"start": v(14.48, 36.5) * mm, "end": v(14.8, 36.35) * mm});
            skLineSegment(sketch, "E379", {"start": v(14.8, 36.35) * mm, "end": v(15.02, 36.12) * mm});
            skLineSegment(sketch, "E380", {"start": v(15.02, 36.12) * mm, "end": v(15.14, 35.84) * mm});
            skLineSegment(sketch, "E381", {"start": v(15.14, 35.84) * mm, "end": v(15.26, 35.84) * mm});
            skLineSegment(sketch, "E382", {"start": v(15.26, 35.84) * mm, "end": v(15.26, 36.9) * mm});
            skLineSegment(sketch, "E383", {"start": v(15.26, 36.9) * mm, "end": v(15.01, 36.93) * mm});
            skLineSegment(sketch, "E384", {"start": v(15.01, 36.93) * mm, "end": v(14.76, 37) * mm});
            skLineSegment(sketch, "E385", {"start": v(14.76, 37) * mm, "end": v(14.46, 37.04) * mm});
            skLineSegment(sketch, "E386", {"start": v(14.46, 37.04) * mm, "end": v(14.07, 37.06) * mm});
            skLineSegment(sketch, "E387", {"start": v(14.07, 37.06) * mm, "end": v(13.39, 36.96) * mm});
            skLineSegment(sketch, "E388", {"start": v(13.39, 36.96) * mm, "end": v(12.88, 36.66) * mm});
            skLineSegment(sketch, "E389", {"start": v(12.88, 36.66) * mm, "end": v(12.56, 36.2) * mm});
            skLineSegment(sketch, "E390", {"start": v(12.56, 36.2) * mm, "end": v(12.45, 35.58) * mm});
            skLineSegment(sketch, "E391", {"start": v(12.45, 35.58) * mm, "end": v(12.53, 35.07) * mm});
            skLineSegment(sketch, "E392", {"start": v(12.53, 35.07) * mm, "end": v(12.75, 34.65) * mm});
            skLineSegment(sketch, "E393", {"start": v(12.75, 34.65) * mm, "end": v(13.07, 34.31) * mm});
            skLineSegment(sketch, "E394", {"start": v(13.07, 34.31) * mm, "end": v(13.46, 34.02) * mm});
            skLineSegment(sketch, "E395", {"start": v(13.46, 34.02) * mm, "end": v(14.1, 33.59) * mm});
            skLineSegment(sketch, "E396", {"start": v(14.1, 33.59) * mm, "end": v(14.57, 33.11) * mm});
            skLineSegment(sketch, "E397", {"start": v(14.57, 33.11) * mm, "end": v(14.72, 32.6) * mm});
            skLineSegment(sketch, "E398", {"start": v(14.72, 32.6) * mm, "end": v(14.65, 32.27) * mm});
            skLineSegment(sketch, "E399", {"start": v(14.65, 32.27) * mm, "end": v(14.46, 32.02) * mm});
            skLineSegment(sketch, "E400", {"start": v(14.46, 32.02) * mm, "end": v(14.18, 31.87) * mm});
            skLineSegment(sketch, "E401", {"start": v(14.18, 31.87) * mm, "end": v(13.83, 31.83) * mm});
            skLineSegment(sketch, "E402", {"start": v(13.83, 31.83) * mm, "end": v(13.4, 31.9) * mm});
            skLineSegment(sketch, "E403", {"start": v(13.4, 31.9) * mm, "end": v(13.04, 32.07) * mm});
            skLineSegment(sketch, "E404", {"start": v(13.04, 32.07) * mm, "end": v(12.75, 32.36) * mm});
            skLineSegment(sketch, "E405", {"start": v(12.75, 32.36) * mm, "end": v(12.6, 32.72) * mm});
            skLineSegment(sketch, "E406", {"start": v(12.6, 32.72) * mm, "end": v(12.48, 32.72) * mm});
            skLineSegment(sketch, "E407", {"start": v(12.48, 32.72) * mm, "end": v(12.48, 31.5) * mm});
            skLineSegment(sketch, "E408", {"start": v(12.48, 31.5) * mm, "end": v(12.7, 31.47) * mm});
            skLineSegment(sketch, "E409", {"start": v(12.7, 31.47) * mm, "end": v(13, 31.39) * mm});
            skLineSegment(sketch, "E410", {"start": v(13, 31.39) * mm, "end": v(13.39, 31.3) * mm});
            skLineSegment(sketch, "E411", {"start": v(13.39, 31.3) * mm, "end": v(13.9, 31.27) * mm});
            skLineSegment(sketch, "E412", {"start": v(13.9, 31.27) * mm, "end": v(14.62, 31.39) * mm});
            skLineSegment(sketch, "E413", {"start": v(14.62, 31.39) * mm, "end": v(15.18, 31.72) * mm});
            skLineSegment(sketch, "E414", {"start": v(15.18, 31.72) * mm, "end": v(15.54, 32.24) * mm});
            skLineSegment(sketch, "E415", {"start": v(15.54, 32.24) * mm, "end": v(15.67, 32.94) * mm});
            skLineSegment(sketch, "E416", {"start": v(15.67, 32.94) * mm, "end": v(15.62, 33.41) * mm});
            skLineSegment(sketch, "E417", {"start": v(15.62, 33.41) * mm, "end": v(15.43, 33.82) * mm});
            skLineSegment(sketch, "E418", {"start": v(15.43, 33.82) * mm, "end": v(15.1, 34.2) * mm});
            skLineSegment(sketch, "E419", {"start": v(15.1, 34.2) * mm, "end": v(14.57, 34.6) * mm});
            skLineSegment(sketch, "E420", {"start": v(11, 34.6) * mm, "end": v(10.46, 34.97) * mm});
            skLineSegment(sketch, "E421", {"start": v(10.46, 34.97) * mm, "end": v(9.93, 35.43) * mm});
            skLineSegment(sketch, "E422", {"start": v(9.93, 35.43) * mm, "end": v(9.77, 35.9) * mm});
            skLineSegment(sketch, "E423", {"start": v(9.77, 35.9) * mm, "end": v(9.82, 36.16) * mm});
            skLineSegment(sketch, "E424", {"start": v(9.82, 36.16) * mm, "end": v(9.95, 36.37) * mm});
            skLineSegment(sketch, "E425", {"start": v(9.95, 36.37) * mm, "end": v(10.19, 36.5) * mm});
            skLineSegment(sketch, "E426", {"start": v(10.19, 36.5) * mm, "end": v(10.53, 36.56) * mm});
            skLineSegment(sketch, "E427", {"start": v(10.53, 36.56) * mm, "end": v(10.91, 36.5) * mm});
            skLineSegment(sketch, "E428", {"start": v(10.91, 36.5) * mm, "end": v(11.23, 36.35) * mm});
            skLineSegment(sketch, "E429", {"start": v(11.23, 36.35) * mm, "end": v(11.46, 36.12) * mm});
            skLineSegment(sketch, "E430", {"start": v(11.46, 36.12) * mm, "end": v(11.58, 35.84) * mm});
            skLineSegment(sketch, "E431", {"start": v(11.58, 35.84) * mm, "end": v(11.7, 35.84) * mm});
            skLineSegment(sketch, "E432", {"start": v(11.7, 35.84) * mm, "end": v(11.7, 36.9) * mm});
            skLineSegment(sketch, "E433", {"start": v(11.7, 36.9) * mm, "end": v(11.45, 36.93) * mm});
            skLineSegment(sketch, "E434", {"start": v(11.45, 36.93) * mm, "end": v(11.2, 37) * mm});
            skLineSegment(sketch, "E435", {"start": v(11.2, 37) * mm, "end": v(10.9, 37.04) * mm});
            skLineSegment(sketch, "E436", {"start": v(10.9, 37.04) * mm, "end": v(10.5, 37.06) * mm});
            skLineSegment(sketch, "E437", {"start": v(10.5, 37.06) * mm, "end": v(9.82, 36.96) * mm});
            skLineSegment(sketch, "E438", {"start": v(9.82, 36.96) * mm, "end": v(9.32, 36.66) * mm});
            skLineSegment(sketch, "E439", {"start": v(9.32, 36.66) * mm, "end": v(9, 36.2) * mm});
            skLineSegment(sketch, "E440", {"start": v(9, 36.2) * mm, "end": v(8.89, 35.58) * mm});
            skLineSegment(sketch, "E441", {"start": v(8.89, 35.58) * mm, "end": v(8.97, 35.07) * mm});
            skLineSegment(sketch, "E442", {"start": v(8.97, 35.07) * mm, "end": v(9.19, 34.65) * mm});
            skLineSegment(sketch, "E443", {"start": v(9.19, 34.65) * mm, "end": v(9.5, 34.31) * mm});
            skLineSegment(sketch, "E444", {"start": v(9.5, 34.31) * mm, "end": v(9.9, 34.02) * mm});
            skLineSegment(sketch, "E445", {"start": v(9.9, 34.02) * mm, "end": v(10.53, 33.59) * mm});
            skLineSegment(sketch, "E446", {"start": v(10.53, 33.59) * mm, "end": v(11, 33.11) * mm});
            skLineSegment(sketch, "E447", {"start": v(11, 33.11) * mm, "end": v(11.15, 32.6) * mm});
            skLineSegment(sketch, "E448", {"start": v(11.15, 32.6) * mm, "end": v(11.08, 32.27) * mm});
            skLineSegment(sketch, "E449", {"start": v(11.08, 32.27) * mm, "end": v(10.9, 32.02) * mm});
            skLineSegment(sketch, "E450", {"start": v(10.9, 32.02) * mm, "end": v(10.61, 31.87) * mm});
            skLineSegment(sketch, "E451", {"start": v(10.61, 31.87) * mm, "end": v(10.27, 31.83) * mm});
            skLineSegment(sketch, "E452", {"start": v(10.27, 31.83) * mm, "end": v(9.84, 31.9) * mm});
            skLineSegment(sketch, "E453", {"start": v(9.84, 31.9) * mm, "end": v(9.47, 32.07) * mm});
            skLineSegment(sketch, "E454", {"start": v(9.47, 32.07) * mm, "end": v(9.19, 32.36) * mm});
            skLineSegment(sketch, "E455", {"start": v(9.19, 32.36) * mm, "end": v(9.04, 32.72) * mm});
            skLineSegment(sketch, "E456", {"start": v(9.04, 32.72) * mm, "end": v(8.91, 32.72) * mm});
            skLineSegment(sketch, "E457", {"start": v(8.91, 32.72) * mm, "end": v(8.91, 31.5) * mm});
            skLineSegment(sketch, "E458", {"start": v(8.91, 31.5) * mm, "end": v(9.13, 31.47) * mm});
            skLineSegment(sketch, "E459", {"start": v(9.13, 31.47) * mm, "end": v(9.43, 31.39) * mm});
            skLineSegment(sketch, "E460", {"start": v(9.43, 31.39) * mm, "end": v(9.82, 31.3) * mm});
            skLineSegment(sketch, "E461", {"start": v(9.82, 31.3) * mm, "end": v(10.33, 31.27) * mm});
            skLineSegment(sketch, "E462", {"start": v(10.33, 31.27) * mm, "end": v(11.05, 31.39) * mm});
            skLineSegment(sketch, "E463", {"start": v(11.05, 31.39) * mm, "end": v(11.61, 31.72) * mm});
            skLineSegment(sketch, "E464", {"start": v(11.61, 31.72) * mm, "end": v(11.98, 32.24) * mm});
            skLineSegment(sketch, "E465", {"start": v(11.98, 32.24) * mm, "end": v(12.1, 32.94) * mm});
            skLineSegment(sketch, "E466", {"start": v(12.1, 32.94) * mm, "end": v(12.05, 33.41) * mm});
            skLineSegment(sketch, "E467", {"start": v(12.05, 33.41) * mm, "end": v(11.87, 33.82) * mm});
            skLineSegment(sketch, "E468", {"start": v(11.87, 33.82) * mm, "end": v(11.53, 34.2) * mm});
            skLineSegment(sketch, "E469", {"start": v(11.53, 34.2) * mm, "end": v(11, 34.6) * mm});
            skLineSegment(sketch, "E470", {"start": v(3.73, 36.86) * mm, "end": v(3.89, 36.7) * mm});
            skLineSegment(sketch, "E471", {"start": v(3.89, 36.7) * mm, "end": v(3.95, 36.28) * mm});
            skLineSegment(sketch, "E472", {"start": v(3.95, 36.28) * mm, "end": v(3.95, 33.39) * mm});
            skLineSegment(sketch, "E473", {"start": v(3.95, 33.39) * mm, "end": v(1.95, 36.98) * mm});
            skLineSegment(sketch, "E474", {"start": v(1.95, 36.98) * mm, "end": v(0.56, 36.98) * mm});
            skLineSegment(sketch, "E475", {"start": v(0.56, 36.98) * mm, "end": v(0.56, 36.86) * mm});
            skLineSegment(sketch, "E476", {"start": v(0.56, 36.86) * mm, "end": v(0.8, 36.7) * mm});
            skLineSegment(sketch, "E477", {"start": v(0.8, 36.7) * mm, "end": v(1, 36.43) * mm});
            skLineSegment(sketch, "E478", {"start": v(1, 36.43) * mm, "end": v(3.87, 31.36) * mm});
            skLineSegment(sketch, "E479", {"start": v(3.87, 31.36) * mm, "end": v(4.56, 31.36) * mm});
            skLineSegment(sketch, "E480", {"start": v(4.56, 31.36) * mm, "end": v(4.56, 36.98) * mm});
            skLineSegment(sketch, "E481", {"start": v(4.56, 36.98) * mm, "end": v(3.73, 36.98) * mm});
            skLineSegment(sketch, "E482", {"start": v(3.73, 36.98) * mm, "end": v(3.73, 36.86) * mm});
            skLineSegment(sketch, "E483", {"start": v(-4.57, 31.98) * mm, "end": v(-4.57, 36.98) * mm});
            skLineSegment(sketch, "E484", {"start": v(-4.57, 36.98) * mm, "end": v(-5.88, 36.98) * mm});
            skLineSegment(sketch, "E485", {"start": v(-5.88, 36.98) * mm, "end": v(-5.88, 36.86) * mm});
            skLineSegment(sketch, "E486", {"start": v(-5.88, 36.86) * mm, "end": v(-5.71, 36.7) * mm});
            skLineSegment(sketch, "E487", {"start": v(-5.71, 36.7) * mm, "end": v(-5.63, 36.28) * mm});
            skLineSegment(sketch, "E488", {"start": v(-5.63, 36.28) * mm, "end": v(-5.63, 31.89) * mm});
            skLineSegment(sketch, "E489", {"start": v(-5.63, 31.89) * mm, "end": v(-5.65, 31.63) * mm});
            skLineSegment(sketch, "E490", {"start": v(-5.65, 31.63) * mm, "end": v(-5.7, 31.47) * mm});
            skLineSegment(sketch, "E491", {"start": v(-5.7, 31.47) * mm, "end": v(-5.7, 31.36) * mm});
            skLineSegment(sketch, "E492", {"start": v(-5.7, 31.36) * mm, "end": v(-4.47, 31.36) * mm});
            skLineSegment(sketch, "E493", {"start": v(-4.47, 31.36) * mm, "end": v(-4.47, 31.47) * mm});
            skLineSegment(sketch, "E494", {"start": v(-4.47, 31.47) * mm, "end": v(-4.53, 31.6) * mm});
            skLineSegment(sketch, "E495", {"start": v(-4.53, 31.6) * mm, "end": v(-4.57, 31.98) * mm});
            skLineSegment(sketch, "E496", {"start": v(-3.01, 34.66) * mm, "end": v(-3.62, 35.78) * mm});
            skLineSegment(sketch, "E497", {"start": v(-3.62, 35.78) * mm, "end": v(-3.62, 31.9) * mm});
            skLineSegment(sketch, "E498", {"start": v(-3.62, 31.9) * mm, "end": v(-3.63, 31.68) * mm});
            skLineSegment(sketch, "E499", {"start": v(-3.63, 31.68) * mm, "end": v(-3.67, 31.47) * mm});
            skLineSegment(sketch, "E500", {"start": v(-3.67, 31.47) * mm, "end": v(-3.67, 31.36) * mm});
            skLineSegment(sketch, "E501", {"start": v(-3.67, 31.36) * mm, "end": v(-2.93, 31.36) * mm});
            skLineSegment(sketch, "E502", {"start": v(-2.93, 31.36) * mm, "end": v(-2.93, 31.47) * mm});
            skLineSegment(sketch, "E503", {"start": v(-2.93, 31.47) * mm, "end": v(-2.99, 31.63) * mm});
            skLineSegment(sketch, "E504", {"start": v(-2.99, 31.63) * mm, "end": v(-3.01, 31.93) * mm});
            skLineSegment(sketch, "E505", {"start": v(-3.01, 31.93) * mm, "end": v(-3.01, 34.66) * mm});
            skLineSegment(sketch, "E506", {"start": v(-7.45, 36.86) * mm, "end": v(-7.28, 36.7) * mm});
            skLineSegment(sketch, "E507", {"start": v(-7.28, 36.7) * mm, "end": v(-7.2, 36.28) * mm});
            skLineSegment(sketch, "E508", {"start": v(-7.2, 36.28) * mm, "end": v(-7.2, 33.15) * mm});
            skLineSegment(sketch, "E509", {"start": v(-7.2, 33.15) * mm, "end": v(-7.23, 32.67) * mm});
            skLineSegment(sketch, "E510", {"start": v(-7.23, 32.67) * mm, "end": v(-7.32, 32.38) * mm});
            skLineSegment(sketch, "E511", {"start": v(-7.32, 32.38) * mm, "end": v(-7.48, 32.17) * mm});
            skLineSegment(sketch, "E512", {"start": v(-7.48, 32.17) * mm, "end": v(-7.69, 32.03) * mm});
            skLineSegment(sketch, "E513", {"start": v(-7.69, 32.03) * mm, "end": v(-7.93, 31.96) * mm});
            skLineSegment(sketch, "E514", {"start": v(-7.93, 31.96) * mm, "end": v(-8.2, 31.94) * mm});
            skLineSegment(sketch, "E515", {"start": v(-8.2, 31.94) * mm, "end": v(-8.44, 31.96) * mm});
            skLineSegment(sketch, "E516", {"start": v(-8.44, 31.96) * mm, "end": v(-8.67, 32.03) * mm});
            skLineSegment(sketch, "E517", {"start": v(-8.67, 32.03) * mm, "end": v(-8.86, 32.17) * mm});
            skLineSegment(sketch, "E518", {"start": v(-8.86, 32.17) * mm, "end": v(-9.02, 32.38) * mm});
            skLineSegment(sketch, "E519", {"start": v(-9.02, 32.38) * mm, "end": v(-9.1, 32.66) * mm});
            skLineSegment(sketch, "E520", {"start": v(-9.1, 32.66) * mm, "end": v(-9.14, 33.11) * mm});
            skLineSegment(sketch, "E521", {"start": v(-9.14, 33.11) * mm, "end": v(-9.14, 36.98) * mm});
            skLineSegment(sketch, "E522", {"start": v(-9.14, 36.98) * mm, "end": v(-10.47, 36.98) * mm});
            skLineSegment(sketch, "E523", {"start": v(-10.47, 36.98) * mm, "end": v(-10.47, 36.86) * mm});
            skLineSegment(sketch, "E524", {"start": v(-10.47, 36.86) * mm, "end": v(-10.3, 36.7) * mm});
            skLineSegment(sketch, "E525", {"start": v(-10.3, 36.7) * mm, "end": v(-10.22, 36.28) * mm});
            skLineSegment(sketch, "E526", {"start": v(-10.22, 36.28) * mm, "end": v(-10.22, 33.14) * mm});
            skLineSegment(sketch, "E527", {"start": v(-10.22, 33.14) * mm, "end": v(-10.2, 32.73) * mm});
            skLineSegment(sketch, "E528", {"start": v(-10.2, 32.73) * mm, "end": v(-10.11, 32.37) * mm});
            skLineSegment(sketch, "E529", {"start": v(-10.11, 32.37) * mm, "end": v(-9.98, 32.05) * mm});
            skLineSegment(sketch, "E530", {"start": v(-9.98, 32.05) * mm, "end": v(-9.78, 31.78) * mm});
            skLineSegment(sketch, "E531", {"start": v(-9.78, 31.78) * mm, "end": v(-9.52, 31.56) * mm});
            skLineSegment(sketch, "E532", {"start": v(-9.52, 31.56) * mm, "end": v(-9.2, 31.4) * mm});
            skLineSegment(sketch, "E533", {"start": v(-9.2, 31.4) * mm, "end": v(-8.8, 31.3) * mm});
            skLineSegment(sketch, "E534", {"start": v(-8.8, 31.3) * mm, "end": v(-8.35, 31.27) * mm});
            skLineSegment(sketch, "E535", {"start": v(-8.35, 31.27) * mm, "end": v(-7.73, 31.34) * mm});
            skLineSegment(sketch, "E536", {"start": v(-7.73, 31.34) * mm, "end": v(-7.24, 31.54) * mm});
            skLineSegment(sketch, "E537", {"start": v(-7.24, 31.54) * mm, "end": v(-6.89, 31.87) * mm});
            skLineSegment(sketch, "E538", {"start": v(-6.89, 31.87) * mm, "end": v(-6.67, 32.33) * mm});
            skLineSegment(sketch, "E539", {"start": v(-6.67, 32.33) * mm, "end": v(-6.59, 32.7) * mm});
            skLineSegment(sketch, "E540", {"start": v(-6.59, 32.7) * mm, "end": v(-6.56, 33.23) * mm});
            skLineSegment(sketch, "E541", {"start": v(-6.56, 33.23) * mm, "end": v(-6.56, 36.98) * mm});
            skLineSegment(sketch, "E542", {"start": v(-6.56, 36.98) * mm, "end": v(-7.45, 36.98) * mm});
            skLineSegment(sketch, "E543", {"start": v(-7.45, 36.98) * mm, "end": v(-7.45, 36.86) * mm});
            skLineSegment(sketch, "E544", {"start": v(-0.83, 36.86) * mm, "end": v(-0.67, 36.7) * mm});
            skLineSegment(sketch, "E545", {"start": v(-0.67, 36.7) * mm, "end": v(-0.61, 36.28) * mm});
            skLineSegment(sketch, "E546", {"start": v(-0.61, 36.28) * mm, "end": v(-0.61, 33.39) * mm});
            skLineSegment(sketch, "E547", {"start": v(-0.61, 33.39) * mm, "end": v(-2.62, 36.98) * mm});
            skLineSegment(sketch, "E548", {"start": v(-2.62, 36.98) * mm, "end": v(-4, 36.98) * mm});
            skLineSegment(sketch, "E549", {"start": v(-4, 36.98) * mm, "end": v(-4, 36.86) * mm});
            skLineSegment(sketch, "E550", {"start": v(-4, 36.86) * mm, "end": v(-3.76, 36.7) * mm});
            skLineSegment(sketch, "E551", {"start": v(-3.76, 36.7) * mm, "end": v(-3.56, 36.43) * mm});
            skLineSegment(sketch, "E552", {"start": v(-3.56, 36.43) * mm, "end": v(-0.69, 31.36) * mm});
            skLineSegment(sketch, "E553", {"start": v(-0.69, 31.36) * mm, "end": v(0, 31.36) * mm});
            skLineSegment(sketch, "E554", {"start": v(0, 31.36) * mm, "end": v(0, 36.98) * mm});
            skLineSegment(sketch, "E555", {"start": v(0, 36.98) * mm, "end": v(-0.83, 36.98) * mm});
            skLineSegment(sketch, "E556", {"start": v(-0.83, 36.98) * mm, "end": v(-0.83, 36.86) * mm});
            skLineSegment(sketch, "E557", {"start": v(7.74, 31.9) * mm, "end": v(6.6, 31.9) * mm});
            skLineSegment(sketch, "E558", {"start": v(6.6, 31.9) * mm, "end": v(6.6, 33.96) * mm});
            skLineSegment(sketch, "E559", {"start": v(6.6, 33.96) * mm, "end": v(7.6, 33.96) * mm});
            skLineSegment(sketch, "E560", {"start": v(7.6, 33.96) * mm, "end": v(7.86, 33.94) * mm});
            skLineSegment(sketch, "E561", {"start": v(7.86, 33.94) * mm, "end": v(8.04, 33.9) * mm});
            skLineSegment(sketch, "E562", {"start": v(8.04, 33.9) * mm, "end": v(8.15, 33.9) * mm});
            skLineSegment(sketch, "E563", {"start": v(8.15, 33.9) * mm, "end": v(8.15, 34.63) * mm});
            skLineSegment(sketch, "E564", {"start": v(8.15, 34.63) * mm, "end": v(8.04, 34.63) * mm});
            skLineSegment(sketch, "E565", {"start": v(8.04, 34.63) * mm, "end": v(7.84, 34.53) * mm});
            skLineSegment(sketch, "E566", {"start": v(7.84, 34.53) * mm, "end": v(7.57, 34.5) * mm});
            skLineSegment(sketch, "E567", {"start": v(7.57, 34.5) * mm, "end": v(6.6, 34.5) * mm});
            skLineSegment(sketch, "E568", {"start": v(6.6, 34.5) * mm, "end": v(6.6, 36.43) * mm});
            skLineSegment(sketch, "E569", {"start": v(6.6, 36.43) * mm, "end": v(7.75, 36.43) * mm});
            skLineSegment(sketch, "E570", {"start": v(7.75, 36.43) * mm, "end": v(8.03, 36.37) * mm});
            skLineSegment(sketch, "E571", {"start": v(8.03, 36.37) * mm, "end": v(8.2, 36.21) * mm});
            skLineSegment(sketch, "E572", {"start": v(8.2, 36.21) * mm, "end": v(8.32, 36.21) * mm});
            skLineSegment(sketch, "E573", {"start": v(8.32, 36.21) * mm, "end": v(8.32, 36.98) * mm});
            skLineSegment(sketch, "E574", {"start": v(8.32, 36.98) * mm, "end": v(5.27, 36.98) * mm});
            skLineSegment(sketch, "E575", {"start": v(5.27, 36.98) * mm, "end": v(5.27, 36.86) * mm});
            skLineSegment(sketch, "E576", {"start": v(5.27, 36.86) * mm, "end": v(5.45, 36.7) * mm});
            skLineSegment(sketch, "E577", {"start": v(5.45, 36.7) * mm, "end": v(5.52, 36.28) * mm});
            skLineSegment(sketch, "E578", {"start": v(5.52, 36.28) * mm, "end": v(5.52, 31.86) * mm});
            skLineSegment(sketch, "E579", {"start": v(5.52, 31.86) * mm, "end": v(5.51, 31.64) * mm});
            skLineSegment(sketch, "E580", {"start": v(5.51, 31.64) * mm, "end": v(5.47, 31.47) * mm});
            skLineSegment(sketch, "E581", {"start": v(5.47, 31.47) * mm, "end": v(5.47, 31.36) * mm});
            skLineSegment(sketch, "E582", {"start": v(5.47, 31.36) * mm, "end": v(8.4, 31.36) * mm});
            skLineSegment(sketch, "E583", {"start": v(8.4, 31.36) * mm, "end": v(8.4, 32.16) * mm});
            skLineSegment(sketch, "E584", {"start": v(8.4, 32.16) * mm, "end": v(8.28, 32.16) * mm});
            skLineSegment(sketch, "E585", {"start": v(8.28, 32.16) * mm, "end": v(8.12, 31.98) * mm});
            skLineSegment(sketch, "E586", {"start": v(8.12, 31.98) * mm, "end": v(7.74, 31.9) * mm});
            skLineSegment(sketch, "E587", {"start": v(-12.6, 34.7) * mm, "end": v(-12.4, 34.6) * mm});
            skLineSegment(sketch, "E588", {"start": v(-12.4, 34.6) * mm, "end": v(-12.29, 34.41) * mm});
            skLineSegment(sketch, "E589", {"start": v(-12.29, 34.41) * mm, "end": v(-12.22, 34.19) * mm});
            skLineSegment(sketch, "E590", {"start": v(-12.22, 34.19) * mm, "end": v(-12.2, 33.96) * mm});
            skLineSegment(sketch, "E591", {"start": v(-12.2, 33.96) * mm, "end": v(-12.2, 31.93) * mm});
            skLineSegment(sketch, "E592", {"start": v(-12.2, 31.93) * mm, "end": v(-12.44, 31.87) * mm});
            skLineSegment(sketch, "E593", {"start": v(-12.44, 31.87) * mm, "end": v(-12.79, 31.84) * mm});
            skLineSegment(sketch, "E594", {"start": v(-12.79, 31.84) * mm, "end": v(-13.47, 32) * mm});
            skLineSegment(sketch, "E595", {"start": v(-13.47, 32) * mm, "end": v(-14.06, 32.53) * mm});
            skLineSegment(sketch, "E596", {"start": v(-14.06, 32.53) * mm, "end": v(-14.47, 33.45) * mm});
            skLineSegment(sketch, "E597", {"start": v(-14.47, 33.45) * mm, "end": v(-14.62, 34.8) * mm});
            skLineSegment(sketch, "E598", {"start": v(-14.62, 34.8) * mm, "end": v(-14.48, 36.09) * mm});
            skLineSegment(sketch, "E599", {"start": v(-14.48, 36.09) * mm, "end": v(-14.1, 36.96) * mm});
            skLineSegment(sketch, "E600", {"start": v(-14.1, 36.96) * mm, "end": v(-13.52, 37.46) * mm});
            skLineSegment(sketch, "E601", {"start": v(-13.52, 37.46) * mm, "end": v(-12.82, 37.62) * mm});
            skLineSegment(sketch, "E602", {"start": v(-12.82, 37.62) * mm, "end": v(-12.38, 37.56) * mm});
            skLineSegment(sketch, "E603", {"start": v(-12.38, 37.56) * mm, "end": v(-12, 37.37) * mm});
            skLineSegment(sketch, "E604", {"start": v(-12, 37.37) * mm, "end": v(-11.7, 37.06) * mm});
            skLineSegment(sketch, "E605", {"start": v(-11.7, 37.06) * mm, "end": v(-11.5, 36.6) * mm});
            skLineSegment(sketch, "E606", {"start": v(-11.5, 36.6) * mm, "end": v(-11.37, 36.6) * mm});
            skLineSegment(sketch, "E607", {"start": v(-11.37, 36.6) * mm, "end": v(-11.37, 38) * mm});
            skLineSegment(sketch, "E608", {"start": v(-11.37, 38) * mm, "end": v(-11.45, 38) * mm});
            skLineSegment(sketch, "E609", {"start": v(-11.45, 38) * mm, "end": v(-11.51, 37.97) * mm});
            skLineSegment(sketch, "E610", {"start": v(-11.51, 37.97) * mm, "end": v(-11.73, 38) * mm});
            skLineSegment(sketch, "E611", {"start": v(-11.73, 38) * mm, "end": v(-12.02, 38.08) * mm});
            skLineSegment(sketch, "E612", {"start": v(-12.02, 38.08) * mm, "end": v(-12.43, 38.15) * mm});
            skLineSegment(sketch, "E613", {"start": v(-12.43, 38.15) * mm, "end": v(-12.97, 38.18) * mm});
            skLineSegment(sketch, "E614", {"start": v(-12.97, 38.18) * mm, "end": v(-14.12, 37.94) * mm});
            skLineSegment(sketch, "E615", {"start": v(-14.12, 37.94) * mm, "end": v(-15.02, 37.24) * mm});
            skLineSegment(sketch, "E616", {"start": v(-15.02, 37.24) * mm, "end": v(-15.6, 36.17) * mm});
            skLineSegment(sketch, "E617", {"start": v(-15.6, 36.17) * mm, "end": v(-15.81, 34.77) * mm});
            skLineSegment(sketch, "E618", {"start": v(-15.81, 34.77) * mm, "end": v(-15.58, 33.21) * mm});
            skLineSegment(sketch, "E619", {"start": v(-15.58, 33.21) * mm, "end": v(-14.96, 32.12) * mm});
            skLineSegment(sketch, "E620", {"start": v(-14.96, 32.12) * mm, "end": v(-14.03, 31.47) * mm});
            skLineSegment(sketch, "E621", {"start": v(-14.03, 31.47) * mm, "end": v(-12.92, 31.25) * mm});
            skLineSegment(sketch, "E622", {"start": v(-12.92, 31.25) * mm, "end": v(-12.22, 31.3) * mm});
            skLineSegment(sketch, "E623", {"start": v(-12.22, 31.3) * mm, "end": v(-11.65, 31.38) * mm});
            skLineSegment(sketch, "E624", {"start": v(-11.65, 31.38) * mm, "end": v(-11.26, 31.48) * mm});
            skLineSegment(sketch, "E625", {"start": v(-11.26, 31.48) * mm, "end": v(-11.09, 31.53) * mm});
            skLineSegment(sketch, "E626", {"start": v(-11.09, 31.53) * mm, "end": v(-11.09, 34.1) * mm});
            skLineSegment(sketch, "E627", {"start": v(-11.09, 34.1) * mm, "end": v(-11.09, 34.27) * mm});
            skLineSegment(sketch, "E628", {"start": v(-11.09, 34.27) * mm, "end": v(-11.08, 34.46) * mm});
            skLineSegment(sketch, "E629", {"start": v(-11.08, 34.46) * mm, "end": v(-11.06, 34.62) * mm});
            skLineSegment(sketch, "E630", {"start": v(-11.06, 34.62) * mm, "end": v(-11.03, 34.7) * mm});
            skLineSegment(sketch, "E631", {"start": v(-11.03, 34.7) * mm, "end": v(-11.03, 34.82) * mm});
            skLineSegment(sketch, "E632", {"start": v(-11.03, 34.82) * mm, "end": v(-12.6, 34.82) * mm});
            skLineSegment(sketch, "E633", {"start": v(-12.6, 34.82) * mm, "end": v(-12.6, 34.7) * mm});
            skLineSegment(sketch, "E634", {"start": v(1.55, 34.66) * mm, "end": v(0.94, 35.78) * mm});
            skLineSegment(sketch, "E635", {"start": v(0.94, 35.78) * mm, "end": v(0.94, 31.9) * mm});
            skLineSegment(sketch, "E636", {"start": v(0.94, 31.9) * mm, "end": v(0.93, 31.68) * mm});
            skLineSegment(sketch, "E637", {"start": v(0.93, 31.68) * mm, "end": v(0.89, 31.47) * mm});
            skLineSegment(sketch, "E638", {"start": v(0.89, 31.47) * mm, "end": v(0.89, 31.36) * mm});
            skLineSegment(sketch, "E639", {"start": v(0.89, 31.36) * mm, "end": v(1.64, 31.36) * mm});
            skLineSegment(sketch, "E640", {"start": v(1.64, 31.36) * mm, "end": v(1.64, 31.47) * mm});
            skLineSegment(sketch, "E641", {"start": v(1.64, 31.47) * mm, "end": v(1.58, 31.63) * mm});
            skLineSegment(sketch, "E642", {"start": v(1.58, 31.63) * mm, "end": v(1.55, 31.93) * mm});
            skLineSegment(sketch, "E643", {"start": v(1.55, 31.93) * mm, "end": v(1.55, 34.66) * mm});
            skLineSegment(sketch, "E644", {"start": v(23.29, 45.91) * mm, "end": v(23.27, 45.77) * mm});
            skLineSegment(sketch, "E645", {"start": v(23.27, 45.77) * mm, "end": v(23.2, 45.37) * mm});
            skLineSegment(sketch, "E646", {"start": v(23.2, 45.37) * mm, "end": v(23.06, 44.82) * mm});
            skLineSegment(sketch, "E647", {"start": v(23.06, 44.82) * mm, "end": v(22.81, 44.18) * mm});
            skLineSegment(sketch, "E648", {"start": v(22.81, 44.18) * mm, "end": v(22.43, 43.54) * mm});
            skLineSegment(sketch, "E649", {"start": v(22.43, 43.54) * mm, "end": v(21.88, 42.99) * mm});
            skLineSegment(sketch, "E650", {"start": v(21.88, 42.99) * mm, "end": v(21.14, 42.6) * mm});
            skLineSegment(sketch, "E651", {"start": v(21.14, 42.6) * mm, "end": v(20.18, 42.44) * mm});
            skLineSegment(sketch, "E652", {"start": v(20.18, 42.44) * mm, "end": v(19.24, 42.54) * mm});
            skLineSegment(sketch, "E653", {"start": v(19.24, 42.54) * mm, "end": v(18.55, 42.79) * mm});
            skLineSegment(sketch, "E654", {"start": v(18.55, 42.79) * mm, "end": v(18.06, 43.16) * mm});
            skLineSegment(sketch, "E655", {"start": v(18.06, 43.16) * mm, "end": v(17.75, 43.6) * mm});
            skLineSegment(sketch, "E656", {"start": v(17.75, 43.6) * mm, "end": v(17.57, 44.1) * mm});
            skLineSegment(sketch, "E657", {"start": v(17.57, 44.1) * mm, "end": v(17.5, 44.58) * mm});
            skLineSegment(sketch, "E658", {"start": v(17.5, 44.58) * mm, "end": v(17.47, 45.03) * mm});
            skLineSegment(sketch, "E659", {"start": v(17.47, 45.03) * mm, "end": v(17.47, 45.4) * mm});
            skLineSegment(sketch, "E660", {"start": v(17.47, 45.4) * mm, "end": v(17.52, 45.82) * mm});
            skLineSegment(sketch, "E661", {"start": v(17.52, 45.82) * mm, "end": v(17.7, 46.43) * mm});
            skLineSegment(sketch, "E662", {"start": v(17.7, 46.43) * mm, "end": v(17.99, 47.15) * mm});
            skLineSegment(sketch, "E663", {"start": v(17.99, 47.15) * mm, "end": v(18.42, 47.91) * mm});
            skLineSegment(sketch, "E664", {"start": v(18.42, 47.91) * mm, "end": v(19, 48.63) * mm});
            skLineSegment(sketch, "E665", {"start": v(19, 48.63) * mm, "end": v(19.73, 49.23) * mm});
            skLineSegment(sketch, "E666", {"start": v(19.73, 49.23) * mm, "end": v(20.62, 49.65) * mm});
            skLineSegment(sketch, "E667", {"start": v(20.62, 49.65) * mm, "end": v(21.7, 49.8) * mm});
            skLineSegment(sketch, "E668", {"start": v(21.7, 49.8) * mm, "end": v(23.29, 49.8) * mm});
            skLineSegment(sketch, "E669", {"start": v(23.29, 49.8) * mm, "end": v(23.29, 45.91) * mm});
            skLineSegment(sketch, "E670", {"start": v(21.38, 52.1) * mm, "end": v(20.35, 51.95) * mm});
            skLineSegment(sketch, "E671", {"start": v(20.35, 51.95) * mm, "end": v(19.24, 51.54) * mm});
            skLineSegment(sketch, "E672", {"start": v(19.24, 51.54) * mm, "end": v(18.12, 50.9) * mm});
            skLineSegment(sketch, "E673", {"start": v(18.12, 50.9) * mm, "end": v(17.07, 50.07) * mm});
            skLineSegment(sketch, "E674", {"start": v(17.07, 50.07) * mm, "end": v(16.13, 49.07) * mm});
            skLineSegment(sketch, "E675", {"start": v(16.13, 49.07) * mm, "end": v(15.38, 47.95) * mm});
            skLineSegment(sketch, "E676", {"start": v(15.38, 47.95) * mm, "end": v(14.88, 46.74) * mm});
            skLineSegment(sketch, "E677", {"start": v(14.88, 46.74) * mm, "end": v(14.7, 45.47) * mm});
            skLineSegment(sketch, "E678", {"start": v(14.7, 45.47) * mm, "end": v(14.8, 44.27) * mm});
            skLineSegment(sketch, "E679", {"start": v(14.8, 44.27) * mm, "end": v(15.05, 43.23) * mm});
            skLineSegment(sketch, "E680", {"start": v(15.05, 43.23) * mm, "end": v(15.46, 42.35) * mm});
            skLineSegment(sketch, "E681", {"start": v(15.46, 42.35) * mm, "end": v(16.02, 41.63) * mm});
            skLineSegment(sketch, "E682", {"start": v(16.02, 41.63) * mm, "end": v(16.72, 41.07) * mm});
            skLineSegment(sketch, "E683", {"start": v(16.72, 41.07) * mm, "end": v(17.53, 40.67) * mm});
            skLineSegment(sketch, "E684", {"start": v(17.53, 40.67) * mm, "end": v(18.46, 40.43) * mm});
            skLineSegment(sketch, "E685", {"start": v(18.46, 40.43) * mm, "end": v(19.48, 40.35) * mm});
            skLineSegment(sketch, "E686", {"start": v(19.48, 40.35) * mm, "end": v(20.45, 40.4) * mm});
            skLineSegment(sketch, "E687", {"start": v(20.45, 40.4) * mm, "end": v(21.23, 40.53) * mm});
            skLineSegment(sketch, "E688", {"start": v(21.23, 40.53) * mm, "end": v(21.84, 40.72) * mm});
            skLineSegment(sketch, "E689", {"start": v(21.84, 40.72) * mm, "end": v(22.3, 40.93) * mm});
            skLineSegment(sketch, "E690", {"start": v(22.3, 40.93) * mm, "end": v(22.64, 41.14) * mm});
            skLineSegment(sketch, "E691", {"start": v(22.64, 41.14) * mm, "end": v(22.85, 41.32) * mm});
            skLineSegment(sketch, "E692", {"start": v(22.85, 41.32) * mm, "end": v(22.97, 41.45) * mm});
            skLineSegment(sketch, "E693", {"start": v(22.97, 41.45) * mm, "end": v(23, 41.5) * mm});
            skLineSegment(sketch, "E694", {"start": v(23, 41.5) * mm, "end": v(23.34, 41.5) * mm});
            skLineSegment(sketch, "E695", {"start": v(23.34, 41.5) * mm, "end": v(23.34, 40.35) * mm});
            skLineSegment(sketch, "E696", {"start": v(23.34, 40.35) * mm, "end": v(25.66, 40.35) * mm});
            skLineSegment(sketch, "E697", {"start": v(25.66, 40.35) * mm, "end": v(25.66, 52.1) * mm});
            skLineSegment(sketch, "E698", {"start": v(25.66, 52.1) * mm, "end": v(21.38, 52.1) * mm});
            skSolve(sketch);
        }
        {
            var Q0;
            Q0=qCreatedBy(id+"F3.planeOp",FACE);
            var sketch = newSketch(context, id + "F9", { "sketchPlane" : qUnion([Q0])});
            skArc(sketch, "E699", {"start": v(-4.57, 60.78) * mm, "mid": v(-3.93, 61.95) * mm, "end": v(-3.49, 63.2) * mm});
            skArc(sketch, "E700", {"start": v(-3.49, 63.2) * mm, "mid": v(-4.13, 62.04) * mm, "end": v(-4.57, 60.78) * mm});
            skArc(sketch, "E701", {"start": v(-4.88, 61.44) * mm, "mid": v(-4.35, 62.4) * mm, "end": v(-3.97, 63.42) * mm});
            skArc(sketch, "E702", {"start": v(-3.97, 63.42) * mm, "mid": v(-4.51, 62.47) * mm, "end": v(-4.88, 61.44) * mm});
            skArc(sketch, "E703", {"start": v(-5.17, 62.04) * mm, "mid": v(-4.72, 62.82) * mm, "end": v(-4.42, 63.67) * mm});
            skArc(sketch, "E704", {"start": v(-4.42, 63.67) * mm, "mid": v(-4.86, 62.88) * mm, "end": v(-5.17, 62.04) * mm});
            skArc(sketch, "E705", {"start": v(-5.42, 62.62) * mm, "mid": v(-5.08, 63.23) * mm, "end": v(-4.84, 63.9) * mm});
            skArc(sketch, "E706", {"start": v(-4.84, 63.9) * mm, "mid": v(-5.2, 63.29) * mm, "end": v(-5.42, 62.62) * mm});
            skArc(sketch, "E707", {"start": v(-4.25, 60.08) * mm, "mid": v(-3.47, 61.49) * mm, "end": v(-2.94, 63) * mm});
            skArc(sketch, "E708", {"start": v(-2.94, 63) * mm, "mid": v(-3.72, 61.6) * mm, "end": v(-4.25, 60.08) * mm});
            skSolve(sketch);
        }
        {
            var Q0;
            Q0=qCreatedBy(id+"F7.planeOp",FACE);
            var sketch = newSketch(context, id + "F10", { "sketchPlane" : qUnion([Q0])});
            skLineSegment(sketch, "E709", {"start": v(-7.7, 43.82) * mm, "end": v(-8, 43.8) * mm});
            skLineSegment(sketch, "E710", {"start": v(-8, 43.8) * mm, "end": v(-8.89, 43.66) * mm});
            skLineSegment(sketch, "E711", {"start": v(-8.89, 43.66) * mm, "end": v(-10.42, 43.3) * mm});
            skLineSegment(sketch, "E712", {"start": v(-10.42, 43.3) * mm, "end": v(-12.61, 42.66) * mm});
            skLineSegment(sketch, "E713", {"start": v(-12.61, 42.66) * mm, "end": v(-13.93, 42.18) * mm});
            skLineSegment(sketch, "E714", {"start": v(-13.93, 42.18) * mm, "end": v(-15.3, 41.63) * mm});
            skLineSegment(sketch, "E715", {"start": v(-15.3, 41.63) * mm, "end": v(-16.66, 41.04) * mm});
            skLineSegment(sketch, "E716", {"start": v(-16.66, 41.04) * mm, "end": v(-17.92, 40.46) * mm});
            skLineSegment(sketch, "E717", {"start": v(-17.92, 40.46) * mm, "end": v(-19.02, 39.93) * mm});
            skLineSegment(sketch, "E718", {"start": v(-19.02, 39.93) * mm, "end": v(-19.9, 39.5) * mm});
            skLineSegment(sketch, "E719", {"start": v(-19.9, 39.5) * mm, "end": v(-20.47, 39.2) * mm});
            skLineSegment(sketch, "E720", {"start": v(-20.47, 39.2) * mm, "end": v(-20.68, 39.1) * mm});
            skLineSegment(sketch, "E721", {"start": v(-20.68, 39.1) * mm, "end": v(-20.49, 39.3) * mm});
            skLineSegment(sketch, "E722", {"start": v(-20.49, 39.3) * mm, "end": v(-19.96, 39.86) * mm});
            skLineSegment(sketch, "E723", {"start": v(-19.96, 39.86) * mm, "end": v(-19.16, 40.68) * mm});
            skLineSegment(sketch, "E724", {"start": v(-19.16, 40.68) * mm, "end": v(-18.14, 41.63) * mm});
            skLineSegment(sketch, "E725", {"start": v(-18.14, 41.63) * mm, "end": v(-16.98, 42.64) * mm});
            skLineSegment(sketch, "E726", {"start": v(-16.98, 42.64) * mm, "end": v(-15.72, 43.58) * mm});
            skLineSegment(sketch, "E727", {"start": v(-15.72, 43.58) * mm, "end": v(-14.44, 44.36) * mm});
            skLineSegment(sketch, "E728", {"start": v(-14.44, 44.36) * mm, "end": v(-13.2, 44.88) * mm});
            skLineSegment(sketch, "E729", {"start": v(-13.2, 44.88) * mm, "end": v(-13.07, 44.8) * mm});
            skLineSegment(sketch, "E730", {"start": v(-13.07, 44.8) * mm, "end": v(-12.72, 44.63) * mm});
            skLineSegment(sketch, "E731", {"start": v(-12.72, 44.63) * mm, "end": v(-12.17, 44.41) * mm});
            skLineSegment(sketch, "E732", {"start": v(-12.17, 44.41) * mm, "end": v(-11.46, 44.2) * mm});
            skLineSegment(sketch, "E733", {"start": v(-11.46, 44.2) * mm, "end": v(-10.63, 44.05) * mm});
            skLineSegment(sketch, "E734", {"start": v(-10.63, 44.05) * mm, "end": v(-9.7, 44.01) * mm});
            skLineSegment(sketch, "E735", {"start": v(-9.7, 44.01) * mm, "end": v(-8.71, 44.16) * mm});
            skLineSegment(sketch, "E736", {"start": v(-8.71, 44.16) * mm, "end": v(-7.7, 44.53) * mm});
            skLineSegment(sketch, "E737", {"start": v(-7.7, 44.53) * mm, "end": v(-7.7, 43.82) * mm});
            skLineSegment(sketch, "E738", {"start": v(24.6, 40.73) * mm, "end": v(24.5, 41.37) * mm});
            skLineSegment(sketch, "E739", {"start": v(24.5, 41.37) * mm, "end": v(24.17, 42.04) * mm});
            skLineSegment(sketch, "E740", {"start": v(24.17, 42.04) * mm, "end": v(23.68, 42.7) * mm});
            skLineSegment(sketch, "E741", {"start": v(23.68, 42.7) * mm, "end": v(23.1, 43.33) * mm});
            skLineSegment(sketch, "E742", {"start": v(23.1, 43.33) * mm, "end": v(22.52, 43.88) * mm});
            skLineSegment(sketch, "E743", {"start": v(22.52, 43.88) * mm, "end": v(22, 44.31) * mm});
            skLineSegment(sketch, "E744", {"start": v(22, 44.31) * mm, "end": v(21.65, 44.6) * mm});
            skLineSegment(sketch, "E745", {"start": v(21.65, 44.6) * mm, "end": v(21.5, 44.7) * mm});
            skLineSegment(sketch, "E746", {"start": v(21.5, 44.7) * mm, "end": v(21.56, 44.7) * mm});
            skLineSegment(sketch, "E747", {"start": v(21.56, 44.7) * mm, "end": v(21.7, 44.68) * mm});
            skLineSegment(sketch, "E748", {"start": v(21.7, 44.68) * mm, "end": v(21.9, 44.66) * mm});
            skLineSegment(sketch, "E749", {"start": v(21.9, 44.66) * mm, "end": v(22.11, 44.67) * mm});
            skLineSegment(sketch, "E750", {"start": v(22.11, 44.67) * mm, "end": v(22.31, 44.71) * mm});
            skLineSegment(sketch, "E751", {"start": v(22.31, 44.71) * mm, "end": v(22.47, 44.8) * mm});
            skLineSegment(sketch, "E752", {"start": v(22.47, 44.8) * mm, "end": v(22.54, 44.95) * mm});
            skLineSegment(sketch, "E753", {"start": v(22.54, 44.95) * mm, "end": v(22.5, 45.17) * mm});
            skLineSegment(sketch, "E754", {"start": v(22.5, 45.17) * mm, "end": v(22.23, 45.45) * mm});
            skLineSegment(sketch, "E755", {"start": v(22.23, 45.45) * mm, "end": v(21.7, 45.75) * mm});
            skLineSegment(sketch, "E756", {"start": v(21.7, 45.75) * mm, "end": v(20.99, 46.05) * mm});
            skLineSegment(sketch, "E757", {"start": v(20.99, 46.05) * mm, "end": v(20.2, 46.34) * mm});
            skLineSegment(sketch, "E758", {"start": v(20.2, 46.34) * mm, "end": v(19.43, 46.6) * mm});
            skLineSegment(sketch, "E759", {"start": v(19.43, 46.6) * mm, "end": v(18.76, 46.8) * mm});
            skLineSegment(sketch, "E760", {"start": v(18.76, 46.8) * mm, "end": v(18.3, 46.93) * mm});
            skLineSegment(sketch, "E761", {"start": v(18.3, 46.93) * mm, "end": v(18.12, 46.98) * mm});
            skLineSegment(sketch, "E762", {"start": v(18.12, 46.98) * mm, "end": v(18.17, 47) * mm});
            skLineSegment(sketch, "E763", {"start": v(18.17, 47) * mm, "end": v(18.3, 47.03) * mm});
            skLineSegment(sketch, "E764", {"start": v(18.3, 47.03) * mm, "end": v(18.47, 47.1) * mm});
            skLineSegment(sketch, "E765", {"start": v(18.47, 47.1) * mm, "end": v(18.66, 47.18) * mm});
            skLineSegment(sketch, "E766", {"start": v(18.66, 47.18) * mm, "end": v(18.83, 47.3) * mm});
            skLineSegment(sketch, "E767", {"start": v(18.83, 47.3) * mm, "end": v(18.96, 47.42) * mm});
            skLineSegment(sketch, "E768", {"start": v(18.96, 47.42) * mm, "end": v(19, 47.57) * mm});
            skLineSegment(sketch, "E769", {"start": v(19, 47.57) * mm, "end": v(18.94, 47.74) * mm});
            skLineSegment(sketch, "E770", {"start": v(18.94, 47.74) * mm, "end": v(18.64, 47.9) * mm});
            skLineSegment(sketch, "E771", {"start": v(18.64, 47.9) * mm, "end": v(18.08, 48) * mm});
            skLineSegment(sketch, "E772", {"start": v(18.08, 48) * mm, "end": v(17.34, 48.07) * mm});
            skLineSegment(sketch, "E773", {"start": v(17.34, 48.07) * mm, "end": v(16.53, 48.12) * mm});
            skLineSegment(sketch, "E774", {"start": v(16.53, 48.12) * mm, "end": v(15.73, 48.14) * mm});
            skLineSegment(sketch, "E775", {"start": v(15.73, 48.14) * mm, "end": v(15.04, 48.15) * mm});
            skLineSegment(sketch, "E776", {"start": v(15.04, 48.15) * mm, "end": v(14.56, 48.15) * mm});
            skLineSegment(sketch, "E777", {"start": v(14.56, 48.15) * mm, "end": v(14.38, 48.15) * mm});
            skLineSegment(sketch, "E778", {"start": v(14.38, 48.15) * mm, "end": v(14.4, 48.17) * mm});
            skLineSegment(sketch, "E779", {"start": v(14.4, 48.17) * mm, "end": v(14.48, 48.23) * mm});
            skLineSegment(sketch, "E780", {"start": v(14.48, 48.23) * mm, "end": v(14.57, 48.31) * mm});
            skLineSegment(sketch, "E781", {"start": v(14.57, 48.31) * mm, "end": v(14.66, 48.42) * mm});
            skLineSegment(sketch, "E782", {"start": v(14.66, 48.42) * mm, "end": v(14.72, 48.54) * mm});
            skLineSegment(sketch, "E783", {"start": v(14.72, 48.54) * mm, "end": v(14.72, 48.67) * mm});
            skLineSegment(sketch, "E784", {"start": v(14.72, 48.67) * mm, "end": v(14.66, 48.8) * mm});
            skLineSegment(sketch, "E785", {"start": v(14.66, 48.8) * mm, "end": v(14.5, 48.9) * mm});
            skLineSegment(sketch, "E786", {"start": v(14.5, 48.9) * mm, "end": v(14.17, 48.98) * mm});
            skLineSegment(sketch, "E787", {"start": v(14.17, 48.98) * mm, "end": v(13.67, 49) * mm});
            skLineSegment(sketch, "E788", {"start": v(13.67, 49) * mm, "end": v(13.07, 48.95) * mm});
            skLineSegment(sketch, "E789", {"start": v(13.07, 48.95) * mm, "end": v(12.44, 48.89) * mm});
            skLineSegment(sketch, "E790", {"start": v(12.44, 48.89) * mm, "end": v(11.83, 48.8) * mm});
            skLineSegment(sketch, "E791", {"start": v(11.83, 48.8) * mm, "end": v(11.3, 48.73) * mm});
            skLineSegment(sketch, "E792", {"start": v(11.3, 48.73) * mm, "end": v(10.95, 48.67) * mm});
            skLineSegment(sketch, "E793", {"start": v(10.95, 48.67) * mm, "end": v(10.82, 48.65) * mm});
            skLineSegment(sketch, "E794", {"start": v(10.82, 48.65) * mm, "end": v(10.86, 48.68) * mm});
            skLineSegment(sketch, "E795", {"start": v(10.86, 48.68) * mm, "end": v(10.95, 48.79) * mm});
            skLineSegment(sketch, "E796", {"start": v(10.95, 48.79) * mm, "end": v(11.07, 48.94) * mm});
            skLineSegment(sketch, "E797", {"start": v(11.07, 48.94) * mm, "end": v(11.17, 49.11) * mm});
            skLineSegment(sketch, "E798", {"start": v(11.17, 49.11) * mm, "end": v(11.22, 49.3) * mm});
            skLineSegment(sketch, "E799", {"start": v(11.22, 49.3) * mm, "end": v(11.18, 49.46) * mm});
            skLineSegment(sketch, "E800", {"start": v(11.18, 49.46) * mm, "end": v(11.02, 49.6) * mm});
            skLineSegment(sketch, "E801", {"start": v(11.02, 49.6) * mm, "end": v(10.7, 49.67) * mm});
            skLineSegment(sketch, "E802", {"start": v(10.7, 49.67) * mm, "end": v(10.2, 49.66) * mm});
            skLineSegment(sketch, "E803", {"start": v(10.2, 49.66) * mm, "end": v(9.6, 49.56) * mm});
            skLineSegment(sketch, "E804", {"start": v(9.6, 49.56) * mm, "end": v(8.92, 49.4) * mm});
            skLineSegment(sketch, "E805", {"start": v(8.92, 49.4) * mm, "end": v(8.24, 49.2) * mm});
            skLineSegment(sketch, "E806", {"start": v(8.24, 49.2) * mm, "end": v(7.6, 49) * mm});
            skLineSegment(sketch, "E807", {"start": v(7.6, 49) * mm, "end": v(7.1, 48.82) * mm});
            skLineSegment(sketch, "E808", {"start": v(7.1, 48.82) * mm, "end": v(6.74, 48.7) * mm});
            skLineSegment(sketch, "E809", {"start": v(6.74, 48.7) * mm, "end": v(6.6, 48.65) * mm});
            skLineSegment(sketch, "E810", {"start": v(6.6, 48.65) * mm, "end": v(6.63, 48.69) * mm});
            skLineSegment(sketch, "E811", {"start": v(6.63, 48.69) * mm, "end": v(6.69, 48.8) * mm});
            skLineSegment(sketch, "E812", {"start": v(6.69, 48.8) * mm, "end": v(6.75, 48.97) * mm});
            skLineSegment(sketch, "E813", {"start": v(6.75, 48.97) * mm, "end": v(6.8, 49.16) * mm});
            skLineSegment(sketch, "E814", {"start": v(6.8, 49.16) * mm, "end": v(6.82, 49.36) * mm});
            skLineSegment(sketch, "E815", {"start": v(6.82, 49.36) * mm, "end": v(6.78, 49.53) * mm});
            skLineSegment(sketch, "E816", {"start": v(6.78, 49.53) * mm, "end": v(6.66, 49.66) * mm});
            skLineSegment(sketch, "E817", {"start": v(6.66, 49.66) * mm, "end": v(6.43, 49.73) * mm});
            skLineSegment(sketch, "E818", {"start": v(6.43, 49.73) * mm, "end": v(6.03, 49.68) * mm});
            skLineSegment(sketch, "E819", {"start": v(6.03, 49.68) * mm, "end": v(5.45, 49.51) * mm});
            skLineSegment(sketch, "E820", {"start": v(5.45, 49.51) * mm, "end": v(4.75, 49.27) * mm});
            skLineSegment(sketch, "E821", {"start": v(4.75, 49.27) * mm, "end": v(4, 49) * mm});
            skLineSegment(sketch, "E822", {"start": v(4, 49) * mm, "end": v(3.26, 48.72) * mm});
            skLineSegment(sketch, "E823", {"start": v(3.26, 48.72) * mm, "end": v(2.61, 48.48) * mm});
            skLineSegment(sketch, "E824", {"start": v(2.61, 48.48) * mm, "end": v(2.11, 48.31) * mm});
            skLineSegment(sketch, "E825", {"start": v(2.11, 48.31) * mm, "end": v(1.83, 48.26) * mm});
            skLineSegment(sketch, "E826", {"start": v(1.83, 48.26) * mm, "end": v(1.58, 48.38) * mm});
            skLineSegment(sketch, "E827", {"start": v(1.58, 48.38) * mm, "end": v(1.46, 48.62) * mm});
            skLineSegment(sketch, "E828", {"start": v(1.46, 48.62) * mm, "end": v(1.52, 48.94) * mm});
            skLineSegment(sketch, "E829", {"start": v(1.52, 48.94) * mm, "end": v(1.83, 49.32) * mm});
            skLineSegment(sketch, "E830", {"start": v(1.83, 49.32) * mm, "end": v(2.5, 49.64) * mm});
            skLineSegment(sketch, "E831", {"start": v(2.5, 49.64) * mm, "end": v(3.4, 49.85) * mm});
            skLineSegment(sketch, "E832", {"start": v(3.4, 49.85) * mm, "end": v(4.2, 50.03) * mm});
            skLineSegment(sketch, "E833", {"start": v(4.2, 50.03) * mm, "end": v(4.56, 50.25) * mm});
            skLineSegment(sketch, "E834", {"start": v(4.56, 50.25) * mm, "end": v(4.54, 50.47) * mm});
            skLineSegment(sketch, "E835", {"start": v(4.54, 50.47) * mm, "end": v(4.44, 50.62) * mm});
            skLineSegment(sketch, "E836", {"start": v(4.44, 50.62) * mm, "end": v(4.32, 50.7) * mm});
            skLineSegment(sketch, "E837", {"start": v(4.32, 50.7) * mm, "end": v(4.27, 50.72) * mm});
            skLineSegment(sketch, "E838", {"start": v(4.27, 50.72) * mm, "end": v(4.42, 50.7) * mm});
            skLineSegment(sketch, "E839", {"start": v(4.42, 50.7) * mm, "end": v(4.8, 50.68) * mm});
            skLineSegment(sketch, "E840", {"start": v(4.8, 50.68) * mm, "end": v(5.36, 50.64) * mm});
            skLineSegment(sketch, "E841", {"start": v(5.36, 50.64) * mm, "end": v(6, 50.62) * mm});
            skLineSegment(sketch, "E842", {"start": v(6, 50.62) * mm, "end": v(6.67, 50.6) * mm});
            skLineSegment(sketch, "E843", {"start": v(6.67, 50.6) * mm, "end": v(7.28, 50.62) * mm});
            skLineSegment(sketch, "E844", {"start": v(7.28, 50.62) * mm, "end": v(7.75, 50.67) * mm});
            skLineSegment(sketch, "E845", {"start": v(7.75, 50.67) * mm, "end": v(8.01, 50.78) * mm});
            skLineSegment(sketch, "E846", {"start": v(8.01, 50.78) * mm, "end": v(8.14, 51.06) * mm});
            skLineSegment(sketch, "E847", {"start": v(8.14, 51.06) * mm, "end": v(8.08, 51.35) * mm});
            skLineSegment(sketch, "E848", {"start": v(8.08, 51.35) * mm, "end": v(7.96, 51.57) * mm});
            skLineSegment(sketch, "E849", {"start": v(7.96, 51.57) * mm, "end": v(7.9, 51.65) * mm});
            skLineSegment(sketch, "E850", {"start": v(7.9, 51.65) * mm, "end": v(8.04, 51.63) * mm});
            skLineSegment(sketch, "E851", {"start": v(8.04, 51.63) * mm, "end": v(8.43, 51.58) * mm});
            skLineSegment(sketch, "E852", {"start": v(8.43, 51.58) * mm, "end": v(9, 51.51) * mm});
            skLineSegment(sketch, "E853", {"start": v(9, 51.51) * mm, "end": v(9.63, 51.45) * mm});
            skLineSegment(sketch, "E854", {"start": v(9.63, 51.45) * mm, "end": v(10.28, 51.4) * mm});
            skLineSegment(sketch, "E855", {"start": v(10.28, 51.4) * mm, "end": v(10.85, 51.4) * mm});
            skLineSegment(sketch, "E856", {"start": v(10.85, 51.4) * mm, "end": v(11.27, 51.46) * mm});
            skLineSegment(sketch, "E857", {"start": v(11.27, 51.46) * mm, "end": v(11.46, 51.6) * mm});
            skLineSegment(sketch, "E858", {"start": v(11.46, 51.6) * mm, "end": v(11.5, 51.95) * mm});
            skLineSegment(sketch, "E859", {"start": v(11.5, 51.95) * mm, "end": v(11.47, 52.27) * mm});
            skLineSegment(sketch, "E860", {"start": v(11.47, 52.27) * mm, "end": v(11.42, 52.5) * mm});
            skLineSegment(sketch, "E861", {"start": v(11.42, 52.5) * mm, "end": v(11.4, 52.59) * mm});
            skLineSegment(sketch, "E862", {"start": v(11.4, 52.59) * mm, "end": v(11.98, 52.55) * mm});
            skLineSegment(sketch, "E863", {"start": v(11.98, 52.55) * mm, "end": v(12.62, 52.52) * mm});
            skLineSegment(sketch, "E864", {"start": v(12.62, 52.52) * mm, "end": v(13.3, 52.5) * mm});
            skLineSegment(sketch, "E865", {"start": v(13.3, 52.5) * mm, "end": v(13.95, 52.52) * mm});
            skLineSegment(sketch, "E866", {"start": v(13.95, 52.52) * mm, "end": v(14.54, 52.55) * mm});
            skLineSegment(sketch, "E867", {"start": v(14.54, 52.55) * mm, "end": v(15.02, 52.62) * mm});
            skLineSegment(sketch, "E868", {"start": v(15.02, 52.62) * mm, "end": v(15.35, 52.73) * mm});
            skLineSegment(sketch, "E869", {"start": v(15.35, 52.73) * mm, "end": v(15.49, 52.88) * mm});
            skLineSegment(sketch, "E870", {"start": v(15.49, 52.88) * mm, "end": v(15.47, 53.07) * mm});
            skLineSegment(sketch, "E871", {"start": v(15.47, 53.07) * mm, "end": v(15.37, 53.28) * mm});
            skLineSegment(sketch, "E872", {"start": v(15.37, 53.28) * mm, "end": v(15.22, 53.5) * mm});
            skLineSegment(sketch, "E873", {"start": v(15.22, 53.5) * mm, "end": v(15.04, 53.7) * mm});
            skLineSegment(sketch, "E874", {"start": v(15.04, 53.7) * mm, "end": v(14.87, 53.88) * mm});
            skLineSegment(sketch, "E875", {"start": v(14.87, 53.88) * mm, "end": v(14.7, 54.03) * mm});
            skLineSegment(sketch, "E876", {"start": v(14.7, 54.03) * mm, "end": v(14.6, 54.13) * mm});
            skLineSegment(sketch, "E877", {"start": v(14.6, 54.13) * mm, "end": v(14.55, 54.17) * mm});
            skLineSegment(sketch, "E878", {"start": v(14.55, 54.17) * mm, "end": v(14.95, 54.21) * mm});
            skLineSegment(sketch, "E879", {"start": v(14.95, 54.21) * mm, "end": v(15.86, 54.32) * mm});
            skLineSegment(sketch, "E880", {"start": v(15.86, 54.32) * mm, "end": v(16.9, 54.44) * mm});
            skLineSegment(sketch, "E881", {"start": v(16.9, 54.44) * mm, "end": v(17.65, 54.52) * mm});
            skLineSegment(sketch, "E882", {"start": v(17.65, 54.52) * mm, "end": v(17.92, 54.55) * mm});
            skLineSegment(sketch, "E883", {"start": v(17.92, 54.55) * mm, "end": v(18.24, 54.6) * mm});
            skLineSegment(sketch, "E884", {"start": v(18.24, 54.6) * mm, "end": v(18.58, 54.68) * mm});
            skLineSegment(sketch, "E885", {"start": v(18.58, 54.68) * mm, "end": v(18.92, 54.79) * mm});
            skLineSegment(sketch, "E886", {"start": v(18.92, 54.79) * mm, "end": v(19.23, 54.91) * mm});
            skLineSegment(sketch, "E887", {"start": v(19.23, 54.91) * mm, "end": v(19.5, 55.07) * mm});
            skLineSegment(sketch, "E888", {"start": v(19.5, 55.07) * mm, "end": v(19.67, 55.25) * mm});
            skLineSegment(sketch, "E889", {"start": v(19.67, 55.25) * mm, "end": v(19.75, 55.45) * mm});
            skLineSegment(sketch, "E890", {"start": v(19.75, 55.45) * mm, "end": v(19.65, 55.9) * mm});
            skLineSegment(sketch, "E891", {"start": v(19.65, 55.9) * mm, "end": v(19.25, 56.39) * mm});
            skLineSegment(sketch, "E892", {"start": v(19.25, 56.39) * mm, "end": v(18.58, 56.91) * mm});
            skLineSegment(sketch, "E893", {"start": v(18.58, 56.91) * mm, "end": v(17.65, 57.5) * mm});
            skLineSegment(sketch, "E894", {"start": v(17.65, 57.5) * mm, "end": v(16.66, 57.93) * mm});
            skLineSegment(sketch, "E895", {"start": v(16.66, 57.93) * mm, "end": v(15.84, 58.1) * mm});
            skLineSegment(sketch, "E896", {"start": v(15.84, 58.1) * mm, "end": v(15.28, 58.1) * mm});
            skLineSegment(sketch, "E897", {"start": v(15.28, 58.1) * mm, "end": v(15.08, 58.08) * mm});
            skLineSegment(sketch, "E898", {"start": v(15.08, 58.08) * mm, "end": v(15.36, 58.29) * mm});
            skLineSegment(sketch, "E899", {"start": v(15.36, 58.29) * mm, "end": v(15.45, 58.52) * mm});
            skLineSegment(sketch, "E900", {"start": v(15.45, 58.52) * mm, "end": v(15.45, 58.7) * mm});
            skLineSegment(sketch, "E901", {"start": v(15.45, 58.7) * mm, "end": v(15.43, 58.78) * mm});
            skLineSegment(sketch, "E902", {"start": v(15.43, 58.78) * mm, "end": v(15.17, 59.07) * mm});
            skLineSegment(sketch, "E903", {"start": v(15.17, 59.07) * mm, "end": v(14.63, 59.22) * mm});
            skLineSegment(sketch, "E904", {"start": v(14.63, 59.22) * mm, "end": v(13.9, 59.26) * mm});
            skLineSegment(sketch, "E905", {"start": v(13.9, 59.26) * mm, "end": v(13.1, 59.21) * mm});
            skLineSegment(sketch, "E906", {"start": v(13.1, 59.21) * mm, "end": v(12.3, 59.12) * mm});
            skLineSegment(sketch, "E907", {"start": v(12.3, 59.12) * mm, "end": v(11.6, 59.02) * mm});
            skLineSegment(sketch, "E908", {"start": v(11.6, 59.02) * mm, "end": v(11.12, 58.93) * mm});
            skLineSegment(sketch, "E909", {"start": v(11.12, 58.93) * mm, "end": v(10.93, 58.9) * mm});
            skLineSegment(sketch, "E910", {"start": v(10.93, 58.9) * mm, "end": v(10.95, 58.94) * mm});
            skLineSegment(sketch, "E911", {"start": v(10.95, 58.94) * mm, "end": v(11, 59.04) * mm});
            skLineSegment(sketch, "E912", {"start": v(11, 59.04) * mm, "end": v(11.03, 59.18) * mm});
            skLineSegment(sketch, "E913", {"start": v(11.03, 59.18) * mm, "end": v(11.01, 59.34) * mm});
            skLineSegment(sketch, "E914", {"start": v(11.01, 59.34) * mm, "end": v(10.92, 59.51) * mm});
            skLineSegment(sketch, "E915", {"start": v(10.92, 59.51) * mm, "end": v(10.7, 59.66) * mm});
            skLineSegment(sketch, "E916", {"start": v(10.7, 59.66) * mm, "end": v(10.36, 59.78) * mm});
            skLineSegment(sketch, "E917", {"start": v(10.36, 59.78) * mm, "end": v(9.82, 59.83) * mm});
            skLineSegment(sketch, "E918", {"start": v(9.82, 59.83) * mm, "end": v(9.17, 59.78) * mm});
            skLineSegment(sketch, "E919", {"start": v(9.17, 59.78) * mm, "end": v(8.52, 59.61) * mm});
            skLineSegment(sketch, "E920", {"start": v(8.52, 59.61) * mm, "end": v(7.9, 59.36) * mm});
            skLineSegment(sketch, "E921", {"start": v(7.9, 59.36) * mm, "end": v(7.32, 59.07) * mm});
            skLineSegment(sketch, "E922", {"start": v(7.32, 59.07) * mm, "end": v(6.82, 58.77) * mm});
            skLineSegment(sketch, "E923", {"start": v(6.82, 58.77) * mm, "end": v(6.43, 58.51) * mm});
            skLineSegment(sketch, "E924", {"start": v(6.43, 58.51) * mm, "end": v(6.17, 58.33) * mm});
            skLineSegment(sketch, "E925", {"start": v(6.17, 58.33) * mm, "end": v(6.08, 58.26) * mm});
            skLineSegment(sketch, "E926", {"start": v(6.08, 58.26) * mm, "end": v(5.71, 58.88) * mm});
            skLineSegment(sketch, "E927", {"start": v(5.71, 58.88) * mm, "end": v(5.17, 59.11) * mm});
            skLineSegment(sketch, "E928", {"start": v(5.17, 59.11) * mm, "end": v(4.52, 59.04) * mm});
            skLineSegment(sketch, "E929", {"start": v(4.52, 59.04) * mm, "end": v(3.83, 58.76) * mm});
            skLineSegment(sketch, "E930", {"start": v(3.83, 58.76) * mm, "end": v(3.18, 58.38) * mm});
            skLineSegment(sketch, "E931", {"start": v(3.18, 58.38) * mm, "end": v(2.63, 57.99) * mm});
            skLineSegment(sketch, "E932", {"start": v(2.63, 57.99) * mm, "end": v(2.25, 57.68) * mm});
            skLineSegment(sketch, "E933", {"start": v(2.25, 57.68) * mm, "end": v(2.1, 57.56) * mm});
            skLineSegment(sketch, "E934", {"start": v(2.1, 57.56) * mm, "end": v(1.78, 58.12) * mm});
            skLineSegment(sketch, "E935", {"start": v(1.78, 58.12) * mm, "end": v(1.24, 58.26) * mm});
            skLineSegment(sketch, "E936", {"start": v(1.24, 58.26) * mm, "end": v(0.57, 58.08) * mm});
            skLineSegment(sketch, "E937", {"start": v(0.57, 58.08) * mm, "end": v(-0.16, 57.7) * mm});
            skLineSegment(sketch, "E938", {"start": v(-0.16, 57.7) * mm, "end": v(-0.87, 57.2) * mm});
            skLineSegment(sketch, "E939", {"start": v(-0.87, 57.2) * mm, "end": v(-1.47, 56.73) * mm});
            skLineSegment(sketch, "E940", {"start": v(-1.47, 56.73) * mm, "end": v(-1.88, 56.36) * mm});
            skLineSegment(sketch, "E941", {"start": v(-1.88, 56.36) * mm, "end": v(-2.04, 56.21) * mm});
            skLineSegment(sketch, "E942", {"start": v(-2.04, 56.21) * mm, "end": v(-2.48, 56.72) * mm});
            skLineSegment(sketch, "E943", {"start": v(-2.48, 56.72) * mm, "end": v(-3.05, 56.78) * mm});
            skLineSegment(sketch, "E944", {"start": v(-3.05, 56.78) * mm, "end": v(-3.7, 56.52) * mm});
            skLineSegment(sketch, "E945", {"start": v(-3.7, 56.52) * mm, "end": v(-4.38, 56.04) * mm});
            skLineSegment(sketch, "E946", {"start": v(-4.38, 56.04) * mm, "end": v(-5, 55.47) * mm});
            skLineSegment(sketch, "E947", {"start": v(-5, 55.47) * mm, "end": v(-5.52, 54.92) * mm});
            skLineSegment(sketch, "E948", {"start": v(-5.52, 54.92) * mm, "end": v(-5.88, 54.5) * mm});
            skLineSegment(sketch, "E949", {"start": v(-5.88, 54.5) * mm, "end": v(-6.01, 54.34) * mm});
            skLineSegment(sketch, "E950", {"start": v(-6.01, 54.34) * mm, "end": v(-6.4, 54.96) * mm});
            skLineSegment(sketch, "E951", {"start": v(-6.4, 54.96) * mm, "end": v(-6.96, 55) * mm});
            skLineSegment(sketch, "E952", {"start": v(-6.96, 55) * mm, "end": v(-7.62, 54.65) * mm});
            skLineSegment(sketch, "E953", {"start": v(-7.62, 54.65) * mm, "end": v(-8.31, 54.03) * mm});
            skLineSegment(sketch, "E954", {"start": v(-8.31, 54.03) * mm, "end": v(-8.97, 53.29) * mm});
            skLineSegment(sketch, "E955", {"start": v(-8.97, 53.29) * mm, "end": v(-9.52, 52.58) * mm});
            skLineSegment(sketch, "E956", {"start": v(-9.52, 52.58) * mm, "end": v(-9.9, 52.04) * mm});
            skLineSegment(sketch, "E957", {"start": v(-9.9, 52.04) * mm, "end": v(-10.04, 51.83) * mm});
            skLineSegment(sketch, "E958", {"start": v(-10.04, 51.83) * mm, "end": v(-10.24, 52.23) * mm});
            skLineSegment(sketch, "E959", {"start": v(-10.24, 52.23) * mm, "end": v(-10.69, 52.31) * mm});
            skLineSegment(sketch, "E960", {"start": v(-10.69, 52.31) * mm, "end": v(-11.4, 51.93) * mm});
            skLineSegment(sketch, "E961", {"start": v(-11.4, 51.93) * mm, "end": v(-12.38, 50.95) * mm});
            skLineSegment(sketch, "E962", {"start": v(-12.38, 50.95) * mm, "end": v(-12.88, 50.23) * mm});
            skLineSegment(sketch, "E963", {"start": v(-12.88, 50.23) * mm, "end": v(-13.24, 49.43) * mm});
            skLineSegment(sketch, "E964", {"start": v(-13.24, 49.43) * mm, "end": v(-13.5, 48.6) * mm});
            skLineSegment(sketch, "E965", {"start": v(-13.5, 48.6) * mm, "end": v(-13.66, 47.78) * mm});
            skLineSegment(sketch, "E966", {"start": v(-13.66, 47.78) * mm, "end": v(-13.76, 47.06) * mm});
            skLineSegment(sketch, "E967", {"start": v(-13.76, 47.06) * mm, "end": v(-13.8, 46.47) * mm});
            skLineSegment(sketch, "E968", {"start": v(-13.8, 46.47) * mm, "end": v(-13.8, 46.07) * mm});
            skLineSegment(sketch, "E969", {"start": v(-13.8, 46.07) * mm, "end": v(-13.8, 45.93) * mm});
            skLineSegment(sketch, "E970", {"start": v(-13.8, 45.93) * mm, "end": v(-14.42, 45.78) * mm});
            skLineSegment(sketch, "E971", {"start": v(-14.42, 45.78) * mm, "end": v(-15.16, 45.38) * mm});
            skLineSegment(sketch, "E972", {"start": v(-15.16, 45.38) * mm, "end": v(-15.8, 44.98) * mm});
            skLineSegment(sketch, "E973", {"start": v(-15.8, 44.98) * mm, "end": v(-16.06, 44.79) * mm});
            skLineSegment(sketch, "E974", {"start": v(-16.06, 44.79) * mm, "end": v(-16, 44.87) * mm});
            skLineSegment(sketch, "E975", {"start": v(-16, 44.87) * mm, "end": v(-15.8, 45.1) * mm});
            skLineSegment(sketch, "E976", {"start": v(-15.8, 45.1) * mm, "end": v(-15.54, 45.46) * mm});
            skLineSegment(sketch, "E977", {"start": v(-15.54, 45.46) * mm, "end": v(-15.2, 45.93) * mm});
            skLineSegment(sketch, "E978", {"start": v(-15.2, 45.93) * mm, "end": v(-14.86, 46.5) * mm});
            skLineSegment(sketch, "E979", {"start": v(-14.86, 46.5) * mm, "end": v(-14.5, 47.13) * mm});
            skLineSegment(sketch, "E980", {"start": v(-14.5, 47.13) * mm, "end": v(-14.2, 47.83) * mm});
            skLineSegment(sketch, "E981", {"start": v(-14.2, 47.83) * mm, "end": v(-13.96, 48.56) * mm});
            skLineSegment(sketch, "E982", {"start": v(-13.96, 48.56) * mm, "end": v(-13.83, 49.28) * mm});
            skLineSegment(sketch, "E983", {"start": v(-13.83, 49.28) * mm, "end": v(-13.82, 49.96) * mm});
            skLineSegment(sketch, "E984", {"start": v(-13.82, 49.96) * mm, "end": v(-13.96, 50.57) * mm});
            skLineSegment(sketch, "E985", {"start": v(-13.96, 50.57) * mm, "end": v(-14.23, 51.1) * mm});
            skLineSegment(sketch, "E986", {"start": v(-14.23, 51.1) * mm, "end": v(-14.65, 51.54) * mm});
            skLineSegment(sketch, "E987", {"start": v(-14.65, 51.54) * mm, "end": v(-15.22, 51.87) * mm});
            skLineSegment(sketch, "E988", {"start": v(-15.22, 51.87) * mm, "end": v(-15.94, 52.07) * mm});
            skLineSegment(sketch, "E989", {"start": v(-15.94, 52.07) * mm, "end": v(-16.83, 52.12) * mm});
            skLineSegment(sketch, "E990", {"start": v(-16.83, 52.12) * mm, "end": v(-17.8, 52) * mm});
            skLineSegment(sketch, "E991", {"start": v(-17.8, 52) * mm, "end": v(-18.75, 51.72) * mm});
            skLineSegment(sketch, "E992", {"start": v(-18.75, 51.72) * mm, "end": v(-19.67, 51.32) * mm});
            skLineSegment(sketch, "E993", {"start": v(-19.67, 51.32) * mm, "end": v(-20.53, 50.83) * mm});
            skLineSegment(sketch, "E994", {"start": v(-20.53, 50.83) * mm, "end": v(-21.3, 50.3) * mm});
            skLineSegment(sketch, "E995", {"start": v(-21.3, 50.3) * mm, "end": v(-21.94, 49.75) * mm});
            skLineSegment(sketch, "E996", {"start": v(-21.94, 49.75) * mm, "end": v(-22.45, 49.23) * mm});
            skLineSegment(sketch, "E997", {"start": v(-22.45, 49.23) * mm, "end": v(-22.78, 48.8) * mm});
            skLineSegment(sketch, "E998", {"start": v(-22.78, 48.8) * mm, "end": v(-22.98, 48.42) * mm});
            skLineSegment(sketch, "E999", {"start": v(-22.98, 48.42) * mm, "end": v(-23.1, 48.09) * mm});
            skLineSegment(sketch, "E1000", {"start": v(-23.1, 48.09) * mm, "end": v(-23.13, 47.81) * mm});
            skLineSegment(sketch, "E1001", {"start": v(-23.13, 47.81) * mm, "end": v(-23.07, 47.62) * mm});
            skLineSegment(sketch, "E1002", {"start": v(-23.07, 47.62) * mm, "end": v(-22.91, 47.5) * mm});
            skLineSegment(sketch, "E1003", {"start": v(-22.91, 47.5) * mm, "end": v(-22.65, 47.48) * mm});
            skLineSegment(sketch, "E1004", {"start": v(-22.65, 47.48) * mm, "end": v(-22.28, 47.58) * mm});
            skLineSegment(sketch, "E1005", {"start": v(-22.28, 47.58) * mm, "end": v(-21.79, 47.8) * mm});
            skLineSegment(sketch, "E1006", {"start": v(-21.79, 47.8) * mm, "end": v(-21.17, 48.04) * mm});
            skLineSegment(sketch, "E1007", {"start": v(-21.17, 48.04) * mm, "end": v(-20.46, 48.2) * mm});
            skLineSegment(sketch, "E1008", {"start": v(-20.46, 48.2) * mm, "end": v(-19.7, 48.28) * mm});
            skLineSegment(sketch, "E1009", {"start": v(-19.7, 48.28) * mm, "end": v(-18.96, 48.32) * mm});
            skLineSegment(sketch, "E1010", {"start": v(-18.96, 48.32) * mm, "end": v(-18.29, 48.32) * mm});
            skLineSegment(sketch, "E1011", {"start": v(-18.29, 48.32) * mm, "end": v(-17.74, 48.3) * mm});
            skLineSegment(sketch, "E1012", {"start": v(-17.74, 48.3) * mm, "end": v(-17.37, 48.28) * mm});
            skLineSegment(sketch, "E1013", {"start": v(-17.37, 48.28) * mm, "end": v(-17.23, 48.26) * mm});
            skLineSegment(sketch, "E1014", {"start": v(-17.23, 48.26) * mm, "end": v(-16.86, 47.66) * mm});
            skLineSegment(sketch, "E1015", {"start": v(-16.86, 47.66) * mm, "end": v(-16.9, 46.77) * mm});
            skLineSegment(sketch, "E1016", {"start": v(-16.9, 46.77) * mm, "end": v(-17.37, 45.56) * mm});
            skLineSegment(sketch, "E1017", {"start": v(-17.37, 45.56) * mm, "end": v(-18.28, 44) * mm});
            skLineSegment(sketch, "E1018", {"start": v(-18.28, 44) * mm, "end": v(-18.99, 43.05) * mm});
            skLineSegment(sketch, "E1019", {"start": v(-18.99, 43.05) * mm, "end": v(-19.9, 42) * mm});
            skLineSegment(sketch, "E1020", {"start": v(-19.9, 42) * mm, "end": v(-20.93, 40.9) * mm});
            skLineSegment(sketch, "E1021", {"start": v(-20.93, 40.9) * mm, "end": v(-21.98, 39.85) * mm});
            skLineSegment(sketch, "E1022", {"start": v(-21.98, 39.85) * mm, "end": v(-22.96, 38.91) * mm});
            skLineSegment(sketch, "E1023", {"start": v(-22.96, 38.91) * mm, "end": v(-23.77, 38.15) * mm});
            skLineSegment(sketch, "E1024", {"start": v(-23.77, 38.15) * mm, "end": v(-24.33, 37.64) * mm});
            skLineSegment(sketch, "E1025", {"start": v(-24.33, 37.64) * mm, "end": v(-24.53, 37.46) * mm});
            skLineSegment(sketch, "E1026", {"start": v(-24.53, 37.46) * mm, "end": v(-24.6, 37.15) * mm});
            skLineSegment(sketch, "E1027", {"start": v(-24.6, 37.15) * mm, "end": v(-24.57, 36.92) * mm});
            skLineSegment(sketch, "E1028", {"start": v(-24.57, 36.92) * mm, "end": v(-24.47, 36.77) * mm});
            skLineSegment(sketch, "E1029", {"start": v(-24.47, 36.77) * mm, "end": v(-24.32, 36.67) * mm});
            skLineSegment(sketch, "E1030", {"start": v(-24.32, 36.67) * mm, "end": v(-24.15, 36.61) * mm});
            skLineSegment(sketch, "E1031", {"start": v(-24.15, 36.61) * mm, "end": v(-24, 36.59) * mm});
            skLineSegment(sketch, "E1032", {"start": v(-24, 36.59) * mm, "end": v(-23.88, 36.58) * mm});
            skLineSegment(sketch, "E1033", {"start": v(-23.88, 36.58) * mm, "end": v(-23.83, 36.58) * mm});
            skLineSegment(sketch, "E1034", {"start": v(-23.83, 36.58) * mm, "end": v(-23.8, 36.08) * mm});
            skLineSegment(sketch, "E1035", {"start": v(-23.8, 36.08) * mm, "end": v(-23.3, 35.97) * mm});
            skLineSegment(sketch, "E1036", {"start": v(-23.3, 35.97) * mm, "end": v(-22.37, 36.25) * mm});
            skLineSegment(sketch, "E1037", {"start": v(-22.37, 36.25) * mm, "end": v(-21.09, 36.93) * mm});
            skLineSegment(sketch, "E1038", {"start": v(-21.09, 36.93) * mm, "end": v(-20.22, 37.4) * mm});
            skLineSegment(sketch, "E1039", {"start": v(-20.22, 37.4) * mm, "end": v(-19.1, 37.9) * mm});
            skLineSegment(sketch, "E1040", {"start": v(-19.1, 37.9) * mm, "end": v(-17.77, 38.43) * mm});
            skLineSegment(sketch, "E1041", {"start": v(-17.77, 38.43) * mm, "end": v(-16.32, 38.95) * mm});
            skLineSegment(sketch, "E1042", {"start": v(-16.32, 38.95) * mm, "end": v(-14.78, 39.43) * mm});
            skLineSegment(sketch, "E1043", {"start": v(-14.78, 39.43) * mm, "end": v(-13.22, 39.86) * mm});
            skLineSegment(sketch, "E1044", {"start": v(-13.22, 39.86) * mm, "end": v(-11.7, 40.2) * mm});
            skLineSegment(sketch, "E1045", {"start": v(-11.7, 40.2) * mm, "end": v(-10.28, 40.44) * mm});
            skLineSegment(sketch, "E1046", {"start": v(-10.28, 40.44) * mm, "end": v(-7.56, 40.61) * mm});
            skLineSegment(sketch, "E1047", {"start": v(-7.56, 40.61) * mm, "end": v(-4.86, 40.46) * mm});
            skLineSegment(sketch, "E1048", {"start": v(-4.86, 40.46) * mm, "end": v(-2.23, 40) * mm});
            skLineSegment(sketch, "E1049", {"start": v(-2.23, 40) * mm, "end": v(0.3, 39.27) * mm});
            skLineSegment(sketch, "E1050", {"start": v(0.3, 39.27) * mm, "end": v(1.63, 38.85) * mm});
            skLineSegment(sketch, "E1051", {"start": v(1.63, 38.85) * mm, "end": v(3.15, 38.47) * mm});
            skLineSegment(sketch, "E1052", {"start": v(3.15, 38.47) * mm, "end": v(4.78, 38.15) * mm});
            skLineSegment(sketch, "E1053", {"start": v(4.78, 38.15) * mm, "end": v(6.45, 37.9) * mm});
            skLineSegment(sketch, "E1054", {"start": v(6.45, 37.9) * mm, "end": v(8.12, 37.72) * mm});
            skLineSegment(sketch, "E1055", {"start": v(8.12, 37.72) * mm, "end": v(9.7, 37.62) * mm});
            skLineSegment(sketch, "E1056", {"start": v(9.7, 37.62) * mm, "end": v(11.15, 37.63) * mm});
            skLineSegment(sketch, "E1057", {"start": v(11.15, 37.63) * mm, "end": v(12.4, 37.75) * mm});
            skLineSegment(sketch, "E1058", {"start": v(12.4, 37.75) * mm, "end": v(13.37, 37.94) * mm});
            skLineSegment(sketch, "E1059", {"start": v(13.37, 37.94) * mm, "end": v(14.08, 38.16) * mm});
            skLineSegment(sketch, "E1060", {"start": v(14.08, 38.16) * mm, "end": v(14.57, 38.4) * mm});
            skLineSegment(sketch, "E1061", {"start": v(14.57, 38.4) * mm, "end": v(14.88, 38.62) * mm});
            skLineSegment(sketch, "E1062", {"start": v(14.88, 38.62) * mm, "end": v(15.02, 38.83) * mm});
            skLineSegment(sketch, "E1063", {"start": v(15.02, 38.83) * mm, "end": v(15.05, 39) * mm});
            skLineSegment(sketch, "E1064", {"start": v(15.05, 39) * mm, "end": v(15, 39.1) * mm});
            skLineSegment(sketch, "E1065", {"start": v(15, 39.1) * mm, "end": v(14.9, 39.15) * mm});
            skLineSegment(sketch, "E1066", {"start": v(14.9, 39.15) * mm, "end": v(14.64, 39.14) * mm});
            skLineSegment(sketch, "E1067", {"start": v(14.64, 39.14) * mm, "end": v(14.09, 39.13) * mm});
            skLineSegment(sketch, "E1068", {"start": v(14.09, 39.13) * mm, "end": v(13.3, 39.13) * mm});
            skLineSegment(sketch, "E1069", {"start": v(13.3, 39.13) * mm, "end": v(12.34, 39.14) * mm});
            skLineSegment(sketch, "E1070", {"start": v(12.34, 39.14) * mm, "end": v(11.25, 39.17) * mm});
            skLineSegment(sketch, "E1071", {"start": v(11.25, 39.17) * mm, "end": v(10.08, 39.25) * mm});
            skLineSegment(sketch, "E1072", {"start": v(10.08, 39.25) * mm, "end": v(8.89, 39.37) * mm});
            skLineSegment(sketch, "E1073", {"start": v(8.89, 39.37) * mm, "end": v(7.72, 39.56) * mm});
            skLineSegment(sketch, "E1074", {"start": v(7.72, 39.56) * mm, "end": v(6.61, 39.82) * mm});
            skLineSegment(sketch, "E1075", {"start": v(6.61, 39.82) * mm, "end": v(5.6, 40.16) * mm});
            skLineSegment(sketch, "E1076", {"start": v(5.6, 40.16) * mm, "end": v(4.7, 40.53) * mm});
            skLineSegment(sketch, "E1077", {"start": v(4.7, 40.53) * mm, "end": v(3.96, 40.92) * mm});
            skLineSegment(sketch, "E1078", {"start": v(3.96, 40.92) * mm, "end": v(3.39, 41.29) * mm});
            skLineSegment(sketch, "E1079", {"start": v(3.39, 41.29) * mm, "end": v(3.03, 41.61) * mm});
            skLineSegment(sketch, "E1080", {"start": v(3.03, 41.61) * mm, "end": v(2.9, 41.87) * mm});
            skLineSegment(sketch, "E1081", {"start": v(2.9, 41.87) * mm, "end": v(3.04, 42.01) * mm});
            skLineSegment(sketch, "E1082", {"start": v(3.04, 42.01) * mm, "end": v(3.85, 42.01) * mm});
            skLineSegment(sketch, "E1083", {"start": v(3.85, 42.01) * mm, "end": v(4.91, 41.79) * mm});
            skLineSegment(sketch, "E1084", {"start": v(4.91, 41.79) * mm, "end": v(5.94, 41.53) * mm});
            skLineSegment(sketch, "E1085", {"start": v(5.94, 41.53) * mm, "end": v(6.6, 41.43) * mm});
            skLineSegment(sketch, "E1086", {"start": v(6.6, 41.43) * mm, "end": v(6.91, 41.57) * mm});
            skLineSegment(sketch, "E1087", {"start": v(6.91, 41.57) * mm, "end": v(7.07, 41.83) * mm});
            skLineSegment(sketch, "E1088", {"start": v(7.07, 41.83) * mm, "end": v(7.13, 42.08) * mm});
            skLineSegment(sketch, "E1089", {"start": v(7.13, 42.08) * mm, "end": v(7.13, 42.19) * mm});
            skLineSegment(sketch, "E1090", {"start": v(7.13, 42.19) * mm, "end": v(7.24, 42.13) * mm});
            skLineSegment(sketch, "E1091", {"start": v(7.24, 42.13) * mm, "end": v(7.52, 41.97) * mm});
            skLineSegment(sketch, "E1092", {"start": v(7.52, 41.97) * mm, "end": v(7.93, 41.75) * mm});
            skLineSegment(sketch, "E1093", {"start": v(7.93, 41.75) * mm, "end": v(8.41, 41.5) * mm});
            skLineSegment(sketch, "E1094", {"start": v(8.41, 41.5) * mm, "end": v(8.91, 41.24) * mm});
            skLineSegment(sketch, "E1095", {"start": v(8.91, 41.24) * mm, "end": v(9.38, 41.03) * mm});
            skLineSegment(sketch, "E1096", {"start": v(9.38, 41.03) * mm, "end": v(9.76, 40.89) * mm});
            skLineSegment(sketch, "E1097", {"start": v(9.76, 40.89) * mm, "end": v(10, 40.84) * mm});
            skLineSegment(sketch, "E1098", {"start": v(10, 40.84) * mm, "end": v(10.12, 40.9) * mm});
            skLineSegment(sketch, "E1099", {"start": v(10.12, 40.9) * mm, "end": v(10.19, 41.04) * mm});
            skLineSegment(sketch, "E1100", {"start": v(10.19, 41.04) * mm, "end": v(10.21, 41.22) * mm});
            skLineSegment(sketch, "E1101", {"start": v(10.21, 41.22) * mm, "end": v(10.2, 41.42) * mm});
            skLineSegment(sketch, "E1102", {"start": v(10.2, 41.42) * mm, "end": v(10.18, 41.62) * mm});
            skLineSegment(sketch, "E1103", {"start": v(10.18, 41.62) * mm, "end": v(10.15, 41.79) * mm});
            skLineSegment(sketch, "E1104", {"start": v(10.15, 41.79) * mm, "end": v(10.13, 41.9) * mm});
            skLineSegment(sketch, "E1105", {"start": v(10.13, 41.9) * mm, "end": v(10.11, 41.95) * mm});
            skLineSegment(sketch, "E1106", {"start": v(10.11, 41.95) * mm, "end": v(10.23, 41.9) * mm});
            skLineSegment(sketch, "E1107", {"start": v(10.23, 41.9) * mm, "end": v(10.55, 41.76) * mm});
            skLineSegment(sketch, "E1108", {"start": v(10.55, 41.76) * mm, "end": v(11, 41.55) * mm});
            skLineSegment(sketch, "E1109", {"start": v(11, 41.55) * mm, "end": v(11.54, 41.33) * mm});
            skLineSegment(sketch, "E1110", {"start": v(11.54, 41.33) * mm, "end": v(12.1, 41.1) * mm});
            skLineSegment(sketch, "E1111", {"start": v(12.1, 41.1) * mm, "end": v(12.63, 40.92) * mm});
            skLineSegment(sketch, "E1112", {"start": v(12.63, 40.92) * mm, "end": v(13.05, 40.8) * mm});
            skLineSegment(sketch, "E1113", {"start": v(13.05, 40.8) * mm, "end": v(13.33, 40.79) * mm});
            skLineSegment(sketch, "E1114", {"start": v(13.33, 40.79) * mm, "end": v(13.47, 40.87) * mm});
            skLineSegment(sketch, "E1115", {"start": v(13.47, 40.87) * mm, "end": v(13.55, 41) * mm});
            skLineSegment(sketch, "E1116", {"start": v(13.55, 41) * mm, "end": v(13.59, 41.19) * mm});
            skLineSegment(sketch, "E1117", {"start": v(13.59, 41.19) * mm, "end": v(13.6, 41.39) * mm});
            skLineSegment(sketch, "E1118", {"start": v(13.6, 41.39) * mm, "end": v(13.57, 41.58) * mm});
            skLineSegment(sketch, "E1119", {"start": v(13.57, 41.58) * mm, "end": v(13.54, 41.74) * mm});
            skLineSegment(sketch, "E1120", {"start": v(13.54, 41.74) * mm, "end": v(13.51, 41.85) * mm});
            skLineSegment(sketch, "E1121", {"start": v(13.51, 41.85) * mm, "end": v(13.5, 41.9) * mm});
            skLineSegment(sketch, "E1122", {"start": v(13.5, 41.9) * mm, "end": v(13.63, 41.83) * mm});
            skLineSegment(sketch, "E1123", {"start": v(13.63, 41.83) * mm, "end": v(13.98, 41.65) * mm});
            skLineSegment(sketch, "E1124", {"start": v(13.98, 41.65) * mm, "end": v(14.49, 41.4) * mm});
            skLineSegment(sketch, "E1125", {"start": v(14.49, 41.4) * mm, "end": v(15.07, 41.14) * mm});
            skLineSegment(sketch, "E1126", {"start": v(15.07, 41.14) * mm, "end": v(15.68, 40.88) * mm});
            skLineSegment(sketch, "E1127", {"start": v(15.68, 40.88) * mm, "end": v(16.24, 40.66) * mm});
            skLineSegment(sketch, "E1128", {"start": v(16.24, 40.66) * mm, "end": v(16.68, 40.54) * mm});
            skLineSegment(sketch, "E1129", {"start": v(16.68, 40.54) * mm, "end": v(16.95, 40.55) * mm});
            skLineSegment(sketch, "E1130", {"start": v(16.95, 40.55) * mm, "end": v(17.14, 40.78) * mm});
            skLineSegment(sketch, "E1131", {"start": v(17.14, 40.78) * mm, "end": v(17.16, 41.05) * mm});
            skLineSegment(sketch, "E1132", {"start": v(17.16, 41.05) * mm, "end": v(17.1, 41.28) * mm});
            skLineSegment(sketch, "E1133", {"start": v(17.1, 41.28) * mm, "end": v(17.07, 41.37) * mm});
            skLineSegment(sketch, "E1134", {"start": v(17.07, 41.37) * mm, "end": v(17.2, 41.29) * mm});
            skLineSegment(sketch, "E1135", {"start": v(17.2, 41.29) * mm, "end": v(17.53, 41.07) * mm});
            skLineSegment(sketch, "E1136", {"start": v(17.53, 41.07) * mm, "end": v(18.02, 40.77) * mm});
            skLineSegment(sketch, "E1137", {"start": v(18.02, 40.77) * mm, "end": v(18.6, 40.42) * mm});
            skLineSegment(sketch, "E1138", {"start": v(18.6, 40.42) * mm, "end": v(19.2, 40.08) * mm});
            skLineSegment(sketch, "E1139", {"start": v(19.2, 40.08) * mm, "end": v(19.78, 39.8) * mm});
            skLineSegment(sketch, "E1140", {"start": v(19.78, 39.8) * mm, "end": v(20.25, 39.6) * mm});
            skLineSegment(sketch, "E1141", {"start": v(20.25, 39.6) * mm, "end": v(20.57, 39.56) * mm});
            skLineSegment(sketch, "E1142", {"start": v(20.57, 39.56) * mm, "end": v(20.75, 39.66) * mm});
            skLineSegment(sketch, "E1143", {"start": v(20.75, 39.66) * mm, "end": v(20.84, 39.86) * mm});
            skLineSegment(sketch, "E1144", {"start": v(20.84, 39.86) * mm, "end": v(20.87, 40.1) * mm});
            skLineSegment(sketch, "E1145", {"start": v(20.87, 40.11) * mm, "end": v(20.85, 40.4) * mm});
            skLineSegment(sketch, "E1146", {"start": v(20.85, 40.4) * mm, "end": v(20.8, 40.67) * mm});
            skLineSegment(sketch, "E1147", {"start": v(20.8, 40.67) * mm, "end": v(20.75, 40.9) * mm});
            skLineSegment(sketch, "E1148", {"start": v(20.75, 40.9) * mm, "end": v(20.7, 41.07) * mm});
            skLineSegment(sketch, "E1149", {"start": v(20.7, 41.07) * mm, "end": v(20.69, 41.14) * mm});
            skLineSegment(sketch, "E1150", {"start": v(20.69, 41.14) * mm, "end": v(21.68, 40.73) * mm});
            skLineSegment(sketch, "E1151", {"start": v(21.68, 40.73) * mm, "end": v(22.5, 40.5) * mm});
            skLineSegment(sketch, "E1152", {"start": v(22.5, 40.5) * mm, "end": v(23.19, 40.42) * mm});
            skLineSegment(sketch, "E1153", {"start": v(23.19, 40.42) * mm, "end": v(23.72, 40.43) * mm});
            skLineSegment(sketch, "E1154", {"start": v(23.72, 40.43) * mm, "end": v(24.12, 40.5) * mm});
            skLineSegment(sketch, "E1155", {"start": v(24.12, 40.5) * mm, "end": v(24.4, 40.6) * mm});
            skLineSegment(sketch, "E1156", {"start": v(24.4, 40.6) * mm, "end": v(24.55, 40.7) * mm});
            skLineSegment(sketch, "E1157", {"start": v(24.55, 40.7) * mm, "end": v(24.6, 40.73) * mm});
            skSolve(sketch);
        }
        {
            var Q0;
            Q0=makeQuery(id+"F10.imprint","IMPRINT",FACE,{"disambiguationData":[TD([[makeQuery(id+"F10.imprint","IMPRINT",EDGE,{"derivedFrom":sQuery(id+"F10.wireOp",EDGE,"E709")}),1.0]])]});
            extrude(context, id + "F11", {"entities" : qUnion([Q0]), "operationType" : NewBodyOperationType.ADD, "endBound" : BoundingType.UP_TO_NEXT, "depth" : 25 * mm});
        }
        {
            var Q0;
            Q0=makeQuery(id+"F8.imprint","IMPRINT",FACE,{"disambiguationData":[TD([[makeQuery(id+"F8.imprint","IMPRINT",EDGE,{"derivedFrom":sQuery(id+"F8.wireOp",EDGE,"E252")}),1.0]])]});
            var Q1;
            Q1=makeQuery(id+"F8.imprint","IMPRINT",FACE,{"disambiguationData":[TD([[makeQuery(id+"F8.imprint","IMPRINT",EDGE,{"derivedFrom":sQuery(id+"F8.wireOp",EDGE,"E234")}),1.0]])]});
            var Q2;
            Q2=makeQuery(id+"F8.imprint","IMPRINT",FACE,{"disambiguationData":[TD([[makeQuery(id+"F8.imprint","IMPRINT",EDGE,{"derivedFrom":sQuery(id+"F8.wireOp",EDGE,"E17")}),1.0]])]});
            var Q3;
            Q3=makeQuery(id+"F8.imprint","IMPRINT",FACE,{"disambiguationData":[TD([[makeQuery(id+"F8.imprint","IMPRINT",EDGE,{"derivedFrom":sQuery(id+"F8.wireOp",EDGE,"E59")}),1.0]])]});
            var Q4;
            Q4=makeQuery(id+"F8.imprint","IMPRINT",FACE,{"disambiguationData":[TD([[makeQuery(id+"F8.imprint","IMPRINT",EDGE,{"derivedFrom":sQuery(id+"F8.wireOp",EDGE,"E114")}),-1.0]])]});
            var Q5;
            Q5=makeQuery(id+"F8.imprint","IMPRINT",FACE,{"disambiguationData":[TD([[makeQuery(id+"F8.imprint","IMPRINT",EDGE,{"derivedFrom":sQuery(id+"F8.wireOp",EDGE,"E118")}),1.0]])]});
            var Q6;
            Q6=makeQuery(id+"F8.imprint","IMPRINT",FACE,{"disambiguationData":[TD([[makeQuery(id+"F8.imprint","IMPRINT",EDGE,{"derivedFrom":sQuery(id+"F8.wireOp",EDGE,"E644")}),1.0]])]});
            var Q7;
            Q7=makeQuery(id+"F8.imprint","IMPRINT",FACE,{"disambiguationData":[TD([[makeQuery(id+"F8.imprint","IMPRINT",EDGE,{"derivedFrom":sQuery(id+"F8.wireOp",EDGE,"E587")}),1.0]])]});
            var Q8;
            Q8=makeQuery(id+"F8.imprint","IMPRINT",FACE,{"disambiguationData":[TD([[makeQuery(id+"F8.imprint","IMPRINT",EDGE,{"derivedFrom":sQuery(id+"F8.wireOp",EDGE,"E506")}),1.0]])]});
            var Q9;
            Q9=makeQuery(id+"F8.imprint","IMPRINT",FACE,{"disambiguationData":[TD([[makeQuery(id+"F8.imprint","IMPRINT",EDGE,{"derivedFrom":sQuery(id+"F8.wireOp",EDGE,"E483")}),1.0]])]});
            var Q10;
            Q10=makeQuery(id+"F8.imprint","IMPRINT",FACE,{"disambiguationData":[TD([[makeQuery(id+"F8.imprint","IMPRINT",EDGE,{"derivedFrom":sQuery(id+"F8.wireOp",EDGE,"E544")}),1.0]])]});
            var Q11;
            Q11=makeQuery(id+"F8.imprint","IMPRINT",FACE,{"disambiguationData":[TD([[makeQuery(id+"F8.imprint","IMPRINT",EDGE,{"derivedFrom":sQuery(id+"F8.wireOp",EDGE,"E496")}),1.0]])]});
            var Q12;
            Q12=makeQuery(id+"F8.imprint","IMPRINT",FACE,{"disambiguationData":[TD([[makeQuery(id+"F8.imprint","IMPRINT",EDGE,{"derivedFrom":sQuery(id+"F8.wireOp",EDGE,"E470")}),1.0]])]});
            var Q13;
            Q13=makeQuery(id+"F8.imprint","IMPRINT",FACE,{"disambiguationData":[TD([[makeQuery(id+"F8.imprint","IMPRINT",EDGE,{"derivedFrom":sQuery(id+"F8.wireOp",EDGE,"E634")}),1.0]])]});
            var Q14;
            Q14=makeQuery(id+"F8.imprint","IMPRINT",FACE,{"disambiguationData":[TD([[makeQuery(id+"F8.imprint","IMPRINT",EDGE,{"derivedFrom":sQuery(id+"F8.wireOp",EDGE,"E557")}),1.0]])]});
            var Q15;
            Q15=makeQuery(id+"F8.imprint","IMPRINT",FACE,{"disambiguationData":[TD([[makeQuery(id+"F8.imprint","IMPRINT",EDGE,{"derivedFrom":sQuery(id+"F8.wireOp",EDGE,"E420")}),1.0]])]});
            var Q16;
            Q16=makeQuery(id+"F8.imprint","IMPRINT",FACE,{"disambiguationData":[TD([[makeQuery(id+"F8.imprint","IMPRINT",EDGE,{"derivedFrom":sQuery(id+"F8.wireOp",EDGE,"E370")}),1.0]])]});
            extrude(context, id + "F12", {"entities" : qUnion([Q0, Q1, Q2, Q3, Q4, Q5, Q6, Q7, Q8, Q9, Q10, Q11, Q12, Q13, Q14, Q15, Q16]), "operationType" : NewBodyOperationType.ADD, "endBound" : BoundingType.UP_TO_NEXT, "oppositeDirection" : true, "depth" : 25 * mm});
        }
        {
            var Q0;
            Q0=qCreatedBy(makeId("Right.planeOp"),FACE);
            var sketch = newSketch(context, id + "F13", { "sketchPlane" : qUnion([Q0])});
            skFitSpline(sketch, "E1158", {"points": [v(-38.08, 79.81) * mm, v(-39.4, 73.24) * mm, v(-40.06, 68.87) * mm, v(-40.02, 64.57) * mm, v(-38.05, 47.1) * mm, v(-30.01, -19.37) * mm, v(-29.7, -22.2) * mm, v(-29.7, -25.96) * mm, v(-33.02, -42.04) * mm, v(-33.47, -47.34) * mm, v(-33.07, -66.83) * mm, v(-31.91, -71.1) * mm, v(-29.46, -74.07) * mm, v(-25.68, -75.16) * mm], "startDerivative": vector(-35.73, -160.8) * mm, "endDerivative": vector(111.11, -2.76) * mm});
            skLineSegment(sketch, "E1159", {"start": v(-39.4, 73.24) * mm, "end": v(-66.79, 73.24) * mm});
            skLineSegment(sketch, "E1160", {"start": v(-66.79, 73.24) * mm, "end": v(-66.79, -81.9) * mm});
            skLineSegment(sketch, "E1161", {"start": v(-66.79, -81.9) * mm, "end": v(-29.7, -81.9) * mm});
            skLineSegment(sketch, "E1162", {"start": v(-29.7, -81.9) * mm, "end": v(-29.46, -74.07) * mm});
            skLineSegment(sketch, "E1163", {"start": v(0, 0) * mm, "end": v(0, -27.6) * mm});
            skSolve(sketch);
        }
        {
            var Q0;
            Q0=makeQuery(id+"F9.imprint","IMPRINT",FACE,{"disambiguationData":[TD([[makeQuery(id+"F9.imprint","IMPRINT",EDGE,{"derivedFrom":sQuery(id+"F9.wireOp",EDGE,"E707")}),1.0]])]});
            var Q1;
            Q1=makeQuery(id+"F9.imprint","IMPRINT",FACE,{"disambiguationData":[TD([[makeQuery(id+"F9.imprint","IMPRINT",EDGE,{"derivedFrom":sQuery(id+"F9.wireOp",EDGE,"E699")}),1.0]])]});
            var Q2;
            Q2=makeQuery(id+"F9.imprint","IMPRINT",FACE,{"disambiguationData":[TD([[makeQuery(id+"F9.imprint","IMPRINT",EDGE,{"derivedFrom":sQuery(id+"F9.wireOp",EDGE,"E701")}),1.0]])]});
            var Q3;
            Q3=makeQuery(id+"F9.imprint","IMPRINT",FACE,{"disambiguationData":[TD([[makeQuery(id+"F9.imprint","IMPRINT",EDGE,{"derivedFrom":sQuery(id+"F9.wireOp",EDGE,"E705")}),1.0]])]});
            var Q4;
            Q4=makeQuery(id+"F9.imprint","IMPRINT",FACE,{"disambiguationData":[TD([[makeQuery(id+"F9.imprint","IMPRINT",EDGE,{"derivedFrom":sQuery(id+"F9.wireOp",EDGE,"E703")}),1.0]])]});
            extrude(context, id + "F14", {"entities" : qUnion([Q0, Q1, Q2, Q3, Q4]), "operationType" : NewBodyOperationType.ADD, "oppositeDirection" : true, "depth" : 14 * mm});
        }
        {
            var Q0;
            Q0=makeQuery(id+"F13.imprint","IMPRINT",FACE,{"disambiguationData":[TD([[makeQuery(id+"F13.imprint","IMPRINT",EDGE,{"derivedFrom":sQuery(id+"F13.wireOp",EDGE,"E1158")}),-1.0]])]});
            var Q1;
            Q1=sQuery(id+"F13.wireOp",EDGE,"E1163");
            revolve(context, id + "F15", {"operationType" : NewBodyOperationType.REMOVE, "entities" : qUnion([Q0]), "axis" : qUnion([Q1]), "revolveType" : RevolveType.FULL, "oppositeDirection" : true});
        }
    });
